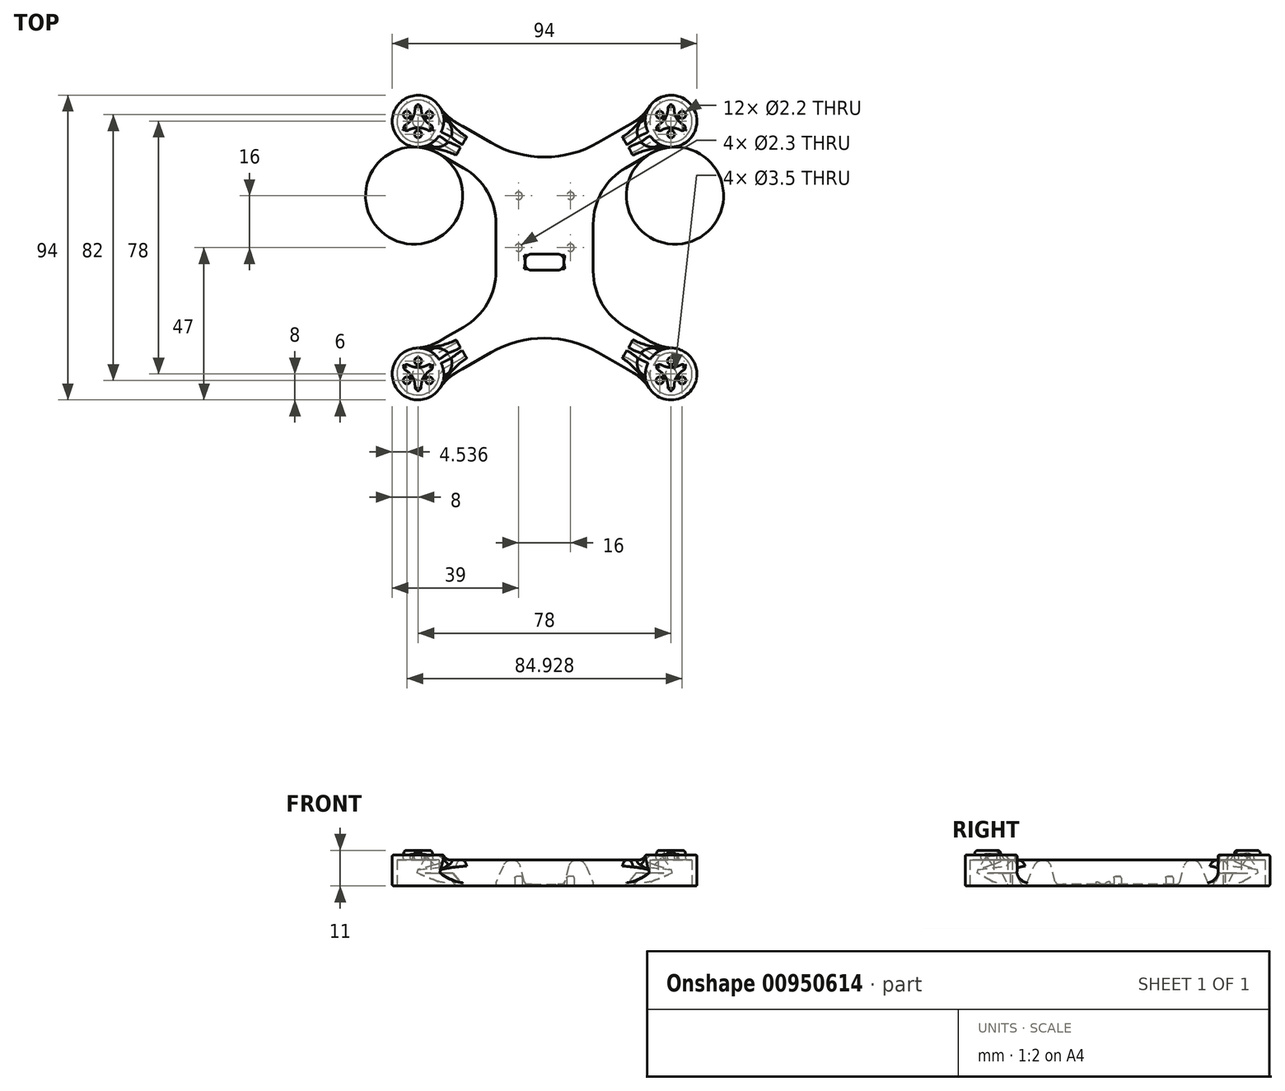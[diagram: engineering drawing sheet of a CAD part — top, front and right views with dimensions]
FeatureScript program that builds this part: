
annotation { "Feature Type Name" : "Feature", "Feature Type Description" : "" }
export const myFeature = defineFeature(function(context is Context, id is Id, definition is map)
    precondition{}
    {
        {
            var Q0;
            Q0=qCreatedBy(makeId("Top.planeOp"),FACE);
            var sketch = newSketch(context, id + "F0", { "sketchPlane" : qUnion([Q0])});
            skLineSegment(sketch, "E0", {"start": v(-31.22, 40.86) * mm, "end": v(0, 22.83) * mm});
            skLineSegment(sketch, "E1", {"start": v(0, 22.83) * mm, "end": v(31.22, 40.86) * mm});
            skLineSegment(sketch, "E2", {"start": v(-31.22, -40.86) * mm, "end": v(0, -22.83) * mm});
            skLineSegment(sketch, "E3", {"start": v(0, -22.83) * mm, "end": v(31.22, -40.86) * mm});
            skLineSegment(sketch, "E4", {"start": v(-36.72, 31.33) * mm, "end": v(-15, 18.8) * mm});
            skLineSegment(sketch, "E5", {"start": v(-15, 18.8) * mm, "end": v(-15, -18.8) * mm});
            skLineSegment(sketch, "E6", {"start": v(-15, -18.8) * mm, "end": v(-36.72, -31.33) * mm});
            skLineSegment(sketch, "E7", {"start": v(36.72, -31.33) * mm, "end": v(15, -18.8) * mm});
            skLineSegment(sketch, "E8", {"start": v(15, -18.8) * mm, "end": v(15, 18.8) * mm});
            skLineSegment(sketch, "E9", {"start": v(15, 18.8) * mm, "end": v(36.72, 31.33) * mm});
            skArc(sketch, "E10", {"start": v(-36.72, 31.33) * mm, "mid": v(-45.93, 43) * mm, "end": v(-31.22, 40.86) * mm});
            skArc(sketch, "E11", {"start": v(36.72, 31.33) * mm, "mid": v(45.93, 43) * mm, "end": v(31.22, 40.86) * mm});
            skArc(sketch, "E12", {"start": v(36.72, -31.33) * mm, "mid": v(45.93, -43) * mm, "end": v(31.22, -40.86) * mm});
            skArc(sketch, "E13", {"start": v(-36.72, -31.33) * mm, "mid": v(-45.93, -43) * mm, "end": v(-31.22, -40.86) * mm});
            skArc(sketch, "E14", {"start": v(-32.55, -38.17) * mm, "mid": v(-44.63, -42.25) * mm, "end": v(-35.05, -33.83) * mm});
            skLineSegment(sketch, "E15", {"start": v(-32.55, -38.17) * mm, "end": v(-35.05, -33.83) * mm});
            skArc(sketch, "E16", {"start": v(32.55, -38.17) * mm, "mid": v(44.63, -42.25) * mm, "end": v(35.05, -33.83) * mm});
            skArc(sketch, "E17", {"start": v(-35.05, 33.83) * mm, "mid": v(-44.63, 42.25) * mm, "end": v(-32.55, 38.17) * mm});
            skArc(sketch, "E18", {"start": v(35.05, 33.83) * mm, "mid": v(44.63, 42.25) * mm, "end": v(32.55, 38.17) * mm});
            skLineSegment(sketch, "E19", {"start": v(-35.05, 33.83) * mm, "end": v(-32.55, 38.17) * mm});
            skLineSegment(sketch, "E20", {"start": v(35.05, 33.83) * mm, "end": v(32.55, 38.17) * mm});
            skLineSegment(sketch, "E21", {"start": v(32.55, -38.17) * mm, "end": v(35.05, -33.83) * mm});
            skSolve(sketch);
        }
        {
            var Q0;
            Q0=qSketchRegion(id+"F0",true);
            extrude(context, id + "F1", {"entities" : qUnion([Q0]), "depth" : 8 * mm, "offsetDistance" : 25 * mm});
        }
        {
            var Q0;
            Q0=qCreatedBy(makeId("Front.planeOp"),FACE);
            var sketch = newSketch(context, id + "F2", { "sketchPlane" : qUnion([Q0])});
            skLineSegment(sketch, "E22.bottom", {"start": v(-6, 10.6) * mm, "end": v(6, 10.6) * mm});
            skLineSegment(sketch, "E22.top", {"start": v(-6, 0.6) * mm, "end": v(6, 0.6) * mm});
            skLineSegment(sketch, "E22.left", {"start": v(-6, 10.6) * mm, "end": v(-6, 0.6) * mm});
            skLineSegment(sketch, "E22.right", {"start": v(6, 10.6) * mm, "end": v(6, 0.6) * mm});
            skSolve(sketch);
        }
        {
            var Q0;
            Q0=qSketchRegion(id+"F2",true);
            extrude(context, id + "F3", {"entities" : qUnion([Q0]), "operationType" : NewBodyOperationType.REMOVE, "oppositeDirection" : true, "depth" : 19 * mm, "offsetDistance" : 25 * mm, "hasSecondDirection" : true, "secondDirectionOppositeDirection" : false, "secondDirectionDepth" : 19 * mm});
        }
        {
            var Q0;
            Q0=makeQuery(id+"F1.opExtrude","CAP_FACE",FACE,{"disambiguationData":[OSD([sQuery(id+"F0.wireOp",EDGE,"E0"),sQuery(id+"F0.wireOp",EDGE,"E1"),sQuery(id+"F0.wireOp",EDGE,"E2"),sQuery(id+"F0.wireOp",EDGE,"E3"),sQuery(id+"F0.wireOp",EDGE,"E4"),sQuery(id+"F0.wireOp",EDGE,"E5"),sQuery(id+"F0.wireOp",EDGE,"E6"),sQuery(id+"F0.wireOp",EDGE,"E7"),sQuery(id+"F0.wireOp",EDGE,"E8"),sQuery(id+"F0.wireOp",EDGE,"E9"),sQuery(id+"F0.wireOp",EDGE,"E10"),sQuery(id+"F0.wireOp",EDGE,"E11"),sQuery(id+"F0.wireOp",EDGE,"E12"),sQuery(id+"F0.wireOp",EDGE,"E13"),sQuery(id+"F0.wireOp",EDGE,"eY3Ntxxg-AOvC-6Sjp-1Sg7-Dh78Z1ENxIpH"),sQuery(id+"F0.wireOp",EDGE,"MyhiPNTX-cIqE-LlnS-pzt5-9fsmOIbbkCBx"),sQuery(id+"F0.wireOp",EDGE,"c5fDbUR1-X0vD-gyia-IhE2-5vfisiyByv1Z"),sQuery(id+"F0.wireOp",EDGE,"z3w7DU23-CNS4-8nrn-3kLT-20PgSTqFnzF7"),sQuery(id+"F0.wireOp",EDGE,"hVG7QURc-v0VO-WvcA-oFbQ-66XRPdHWUu1N"),sQuery(id+"F0.wireOp",EDGE,"sfXvGUbo-ry80-gNXO-uOhN-L8BNUFceVqag"),sQuery(id+"F0.wireOp",EDGE,"QFO76mAv-pKme-nUwV-aMAa-C3MPOYOEvzGl"),sQuery(id+"F0.wireOp",EDGE,"fpymSL76-tXuZ-IzAU-FBSV-KsOygqMtrIGQ")])],"isStart":false});
            var sketch = newSketch(context, id + "F4", { "sketchPlane" : qUnion([Q0])});
            skCircle(sketch, "E23", {"center": v(-39, 39) * mm, "radius": 8 * mm});
            skCircle(sketch, "E24", {"center": v(39, 39) * mm, "radius": 8 * mm});
            skCircle(sketch, "E25", {"center": v(39, -39) * mm, "radius": 8 * mm});
            skCircle(sketch, "E26", {"center": v(-39, -39) * mm, "radius": 8 * mm});
            skSolve(sketch);
        }
        {
            var Q0;
            Q0=qSketchRegion(id+"F4",true);
            extrude(context, id + "F5", {"entities" : qUnion([Q0]), "operationType" : NewBodyOperationType.ADD, "depth" : 3 * mm, "offsetDistance" : 25 * mm});
        }
        {
            var Q0;
            Q0=makeQuery(id+"F5.opExtrude","CAP_FACE",FACE,{"disambiguationData":[OSD([sQuery(id+"F4.wireOp",EDGE,"E23")])],"isStart":false});
            var sketch = newSketch(context, id + "F6", { "sketchPlane" : qUnion([Q0])});
            skCircle(sketch, "E27", {"center": v(-39, 39) * mm, "radius": 8 * mm});
            skArc(sketch, "E28", {"start": v(-43.74, 37.41) * mm, "mid": v(-40.73, 40) * mm, "end": v(-40, 43.9) * mm});
            skArc(sketch, "E29.1.0", {"start": v(-35.25, 35.69) * mm, "mid": v(-39, 37) * mm, "end": v(-42.75, 35.69) * mm});
            skArc(sketch, "E29.2.0", {"start": v(-38, 43.9) * mm, "mid": v(-37.27, 40) * mm, "end": v(-34.26, 37.41) * mm});
            skArc(sketch, "E30", {"start": v(-34.26, 37.41) * mm, "mid": v(-34.67, 36.5) * mm, "end": v(-35.25, 35.69) * mm});
            skArc(sketch, "E31", {"start": v(-38, 43.9) * mm, "mid": v(-39, 44) * mm, "end": v(-40, 43.9) * mm});
            skArc(sketch, "E32", {"start": v(-42.75, 35.69) * mm, "mid": v(-43.33, 36.5) * mm, "end": v(-43.74, 37.41) * mm});
            skCircle(sketch, "E33.MirrorC", {"center": v(39, 39) * mm, "radius": 8 * mm});
            skArc(sketch, "E34.MirrorCS", {"start": v(35.25, 35.69) * mm, "mid": v(39, 37) * mm, "end": v(42.75, 35.69) * mm});
            skArc(sketch, "E35.MirrorCS", {"start": v(34.26, 37.41) * mm, "mid": v(34.67, 36.5) * mm, "end": v(35.25, 35.69) * mm});
            skArc(sketch, "E36.MirrorCS", {"start": v(38, 43.9) * mm, "mid": v(37.27, 40) * mm, "end": v(34.26, 37.41) * mm});
            skArc(sketch, "E37.MirrorCS", {"start": v(43.74, 37.41) * mm, "mid": v(40.73, 40) * mm, "end": v(40, 43.9) * mm});
            skArc(sketch, "E38.MirrorCS", {"start": v(42.75, 35.69) * mm, "mid": v(43.33, 36.5) * mm, "end": v(43.74, 37.41) * mm});
            skArc(sketch, "E39.MirrorCS", {"start": v(38, 43.9) * mm, "mid": v(39, 44) * mm, "end": v(40, 43.9) * mm});
            skArc(sketch, "E40.MirrorCS", {"start": v(-35.25, -35.69) * mm, "mid": v(-39, -37) * mm, "end": v(-42.75, -35.69) * mm});
            skArc(sketch, "E41.MirrorCS", {"start": v(38, -43.9) * mm, "mid": v(37.27, -40) * mm, "end": v(34.26, -37.41) * mm});
            skArc(sketch, "E42.MirrorCS", {"start": v(-42.75, -35.69) * mm, "mid": v(-43.33, -36.5) * mm, "end": v(-43.74, -37.41) * mm});
            skArc(sketch, "E43.MirrorCS", {"start": v(-43.74, -37.41) * mm, "mid": v(-40.73, -40) * mm, "end": v(-40, -43.9) * mm});
            skArc(sketch, "E44.MirrorCS", {"start": v(35.25, -35.69) * mm, "mid": v(39, -37) * mm, "end": v(42.75, -35.69) * mm});
            skArc(sketch, "E45.MirrorCS", {"start": v(38, -43.9) * mm, "mid": v(39, -44) * mm, "end": v(40, -43.9) * mm});
            skArc(sketch, "E46.MirrorCS", {"start": v(-38, -43.9) * mm, "mid": v(-37.27, -40) * mm, "end": v(-34.26, -37.41) * mm});
            skArc(sketch, "E47.MirrorCS", {"start": v(43.74, -37.41) * mm, "mid": v(40.73, -40) * mm, "end": v(40, -43.9) * mm});
            skArc(sketch, "E48.MirrorCS", {"start": v(42.75, -35.69) * mm, "mid": v(43.33, -36.5) * mm, "end": v(43.74, -37.41) * mm});
            skArc(sketch, "E49.MirrorCS", {"start": v(34.26, -37.41) * mm, "mid": v(34.67, -36.5) * mm, "end": v(35.25, -35.69) * mm});
            skArc(sketch, "E50.MirrorCS", {"start": v(-38, -43.9) * mm, "mid": v(-39, -44) * mm, "end": v(-40, -43.9) * mm});
            skArc(sketch, "E51.MirrorCS", {"start": v(-34.26, -37.41) * mm, "mid": v(-34.67, -36.5) * mm, "end": v(-35.25, -35.69) * mm});
            skCircle(sketch, "E52.MirrorC", {"center": v(-39, -39) * mm, "radius": 8 * mm});
            skCircle(sketch, "E53.MirrorC", {"center": v(39, -39) * mm, "radius": 8 * mm});
            skSolve(sketch);
        }
        {
            var Q0;
            Q0 = qSketchRegion(id + "F6", true);
            extrude(context, id + "F7", {"entities" : qUnion([Q0]), "operationType" : NewBodyOperationType.REMOVE, "oppositeDirection" : true, "depth" : 1.4 * mm, "offsetDistance" : 25 * mm});
        }
        {
            var Q0;
            Q0=makeQuery(id+"F7.boolean.opBoolean","COPY",FACE,{"derivedFrom":makeQuery(id+"F7.opExtrude","CAP_FACE",FACE,{"disambiguationData":[OSD([sQuery(id+"F6.wireOp",EDGE,"E27"),sQuery(id+"F6.wireOp",EDGE,"E28"),sQuery(id+"F6.wireOp",EDGE,"E29.1.0"),sQuery(id+"F6.wireOp",EDGE,"E29.2.0"),sQuery(id+"F6.wireOp",EDGE,"E30"),sQuery(id+"F6.wireOp",EDGE,"E31"),sQuery(id+"F6.wireOp",EDGE,"E32")])],"isStart":false})});
            var sketch = newSketch(context, id + "F8", { "sketchPlane" : qUnion([Q0])});
            skCircle(sketch, "E54", {"center": v(-42.46, 41) * mm, "radius": 1.1 * mm});
            skCircle(sketch, "E55.1.0", {"center": v(-39, 35) * mm, "radius": 1.1 * mm});
            skCircle(sketch, "E55.2.0", {"center": v(-35.54, 41) * mm, "radius": 1.1 * mm});
            skPoint(sketch, "E55.center", {"position": v(-39, 39) * mm});
            skCircle(sketch, "E56.MirrorC", {"center": v(39, 35) * mm, "radius": 1.1 * mm});
            skCircle(sketch, "E57.MirrorC", {"center": v(35.54, 41) * mm, "radius": 1.1 * mm});
            skCircle(sketch, "E58.MirrorC", {"center": v(42.46, 41) * mm, "radius": 1.1 * mm});
            skPoint(sketch, "E59.MirrorP", {"position": v(39, 39) * mm});
            skCircle(sketch, "E60.MirrorC", {"center": v(-35.54, -41) * mm, "radius": 1.1 * mm});
            skCircle(sketch, "E61.MirrorC", {"center": v(-42.46, -41) * mm, "radius": 1.1 * mm});
            skCircle(sketch, "E62.MirrorC", {"center": v(35.54, -41) * mm, "radius": 1.1 * mm});
            skCircle(sketch, "E63.MirrorC", {"center": v(42.46, -41) * mm, "radius": 1.1 * mm});
            skCircle(sketch, "E64.MirrorC", {"center": v(-39, -35) * mm, "radius": 1.1 * mm});
            skCircle(sketch, "E65.MirrorC", {"center": v(39, -35) * mm, "radius": 1.1 * mm});
            skPoint(sketch, "E66.MirrorP", {"position": v(39, -39) * mm});
            skPoint(sketch, "E67.MirrorP", {"position": v(-39, -39) * mm});
            skSolve(sketch);
        }
        {
            var Q0;
            Q0 = qSketchRegion(id + "F8", true);
            extrude(context, id + "F9", {"entities" : qUnion([Q0]), "operationType" : NewBodyOperationType.REMOVE, "oppositeDirection" : true, "depth" : 3 * mm, "offsetDistance" : 25 * mm});
        }
        {
            var Q0;
            Q0=qCreatedBy(makeId("Top.planeOp"),FACE);
            var sketch = newSketch(context, id + "F10", { "sketchPlane" : qUnion([Q0])});
            skCircle(sketch, "E68", {"center": v(8, 16) * mm, "radius": 1.15 * mm});
            skCircle(sketch, "E69", {"center": v(-8, 16) * mm, "radius": 1.15 * mm});
            skCircle(sketch, "E70", {"center": v(-8, 0) * mm, "radius": 1.15 * mm});
            skCircle(sketch, "E71", {"center": v(8, 0) * mm, "radius": 1.15 * mm});
            skLineSegment(sketch, "E72.bottom", {"start": v(-4, -7) * mm, "end": v(4, -7) * mm});
            skLineSegment(sketch, "E72.top", {"start": v(-4, -2) * mm, "end": v(4, -2) * mm});
            skLineSegment(sketch, "E72.left", {"start": v(-6, -5) * mm, "end": v(-6, -4) * mm});
            skLineSegment(sketch, "E72.right", {"start": v(6, -5) * mm, "end": v(6, -4) * mm});
            skPoint(sketch, "E73.visualSharp", {"position": v(-6, -7) * mm});
            skArc(sketch, "E73.filletArc", {"start": v(-6, -5) * mm, "mid": v(-5.41, -6.41) * mm, "end": v(-4, -7) * mm});
            skPoint(sketch, "E74.visualSharp", {"position": v(-6, -2) * mm});
            skArc(sketch, "E74.filletArc", {"start": v(-4, -2) * mm, "mid": v(-5.41, -2.59) * mm, "end": v(-6, -4) * mm});
            skPoint(sketch, "E75.visualSharp", {"position": v(6, -7) * mm});
            skArc(sketch, "E75.filletArc", {"start": v(4, -7) * mm, "mid": v(5.41, -6.41) * mm, "end": v(6, -5) * mm});
            skPoint(sketch, "E76.visualSharp", {"position": v(6, -2) * mm});
            skArc(sketch, "E76.filletArc", {"start": v(6, -4) * mm, "mid": v(5.41, -2.59) * mm, "end": v(4, -2) * mm});
            skSolve(sketch);
        }
        {
            var Q0;
            Q0 = qSketchRegion(id + "F10", true);
            extrude(context, id + "F11", {"entities" : qUnion([Q0]), "operationType" : NewBodyOperationType.REMOVE, "depth" : 3 * mm, "offsetDistance" : 25 * mm});
        }
        {
            var Q0;
            Q0=makeQuery(id+"F5.opExtrude","CAP_FACE",FACE,{"disambiguationData":[OSD([sQuery(id+"F4.wireOp",EDGE,"E26")])],"isStart":true});
            var sketch = newSketch(context, id + "F12", { "sketchPlane" : qUnion([Q0])});
            skCircle(sketch, "E77", {"center": v(-39, 39) * mm, "radius": 1.75 * mm});
            skCircle(sketch, "E78.MirrorC", {"center": v(39, 39) * mm, "radius": 1.75 * mm});
            skCircle(sketch, "E79.MirrorC", {"center": v(-39, -39) * mm, "radius": 1.75 * mm});
            skCircle(sketch, "E80.MirrorC", {"center": v(39, -39) * mm, "radius": 1.75 * mm});
            skSolve(sketch);
        }
        {
            var Q0;
            Q0 = qSketchRegion(id + "F12", true);
            extrude(context, id + "F13", {"entities" : qUnion([Q0]), "operationType" : NewBodyOperationType.REMOVE, "oppositeDirection" : true, "depth" : 2 * mm, "offsetDistance" : 25 * mm});
        }
        {
            var Q0;
            Q0=qCreatedBy(makeId("Top.planeOp"),FACE);
            var sketch = newSketch(context, id + "F14", { "sketchPlane" : qUnion([Q0])});
            skLineSegment(sketch, "E81", {"start": v(-32.55, -38.17) * mm, "end": v(-23.9, -33.17) * mm});
            skLineSegment(sketch, "E82", {"start": v(-23.9, -33.17) * mm, "end": v(-26.4, -28.83) * mm});
            skLineSegment(sketch, "E83", {"start": v(-26.4, -28.83) * mm, "end": v(-35.05, -33.83) * mm});
            skLineSegment(sketch, "E84", {"start": v(-35.05, -33.83) * mm, "end": v(-32.55, -38.17) * mm});
            skLineSegment(sketch, "E85.MirrorCS", {"start": v(-23.9, 33.17) * mm, "end": v(-26.4, 28.83) * mm});
            skLineSegment(sketch, "E86.MirrorCS", {"start": v(-32.55, 38.17) * mm, "end": v(-23.9, 33.17) * mm});
            skLineSegment(sketch, "E87.MirrorCS", {"start": v(-35.05, 33.83) * mm, "end": v(-32.55, 38.17) * mm});
            skLineSegment(sketch, "E88.MirrorCS", {"start": v(-26.4, 28.83) * mm, "end": v(-35.05, 33.83) * mm});
            skLineSegment(sketch, "E89.MirrorCS", {"start": v(35.05, -33.83) * mm, "end": v(32.55, -38.17) * mm});
            skLineSegment(sketch, "E90.MirrorCS", {"start": v(35.05, 33.83) * mm, "end": v(32.55, 38.17) * mm});
            skLineSegment(sketch, "E91.MirrorCS", {"start": v(23.9, -33.17) * mm, "end": v(26.4, -28.83) * mm});
            skLineSegment(sketch, "E92.MirrorCS", {"start": v(23.9, 33.17) * mm, "end": v(26.4, 28.83) * mm});
            skLineSegment(sketch, "E93.MirrorCS", {"start": v(32.55, -38.17) * mm, "end": v(23.9, -33.17) * mm});
            skLineSegment(sketch, "E94.MirrorCS", {"start": v(26.4, -28.83) * mm, "end": v(35.05, -33.83) * mm});
            skLineSegment(sketch, "E95.MirrorCS", {"start": v(26.4, 28.83) * mm, "end": v(35.05, 33.83) * mm});
            skLineSegment(sketch, "E96.MirrorCS", {"start": v(32.55, 38.17) * mm, "end": v(23.9, 33.17) * mm});
            skSolve(sketch);
        }
        {
            var Q0;
            Q0 = qSketchRegion(id + "F14", true);
            extrude(context, id + "F15", {"entities" : qUnion([Q0]), "operationType" : NewBodyOperationType.REMOVE, "depth" : 4 * mm, "offsetDistance" : 25 * mm});
        }
        {
            var Q0;
            Q0=makeQuery(id+"F15.boolean.opBoolean","COPY",EDGE,{"derivedFrom":makeQuery(id+"F15.opExtrude","CAP_EDGE",EDGE,{"disambiguationData":[OSD([sQuery(id+"F14.wireOp",EDGE,"E84")])],"isStart":false})});
            var Q1;
            Q1=makeQuery(id+"F15.boolean.opBoolean","COPY",EDGE,{"derivedFrom":makeQuery(id+"F15.opExtrude","CAP_EDGE",EDGE,{"disambiguationData":[OSD([sQuery(id+"F14.wireOp",EDGE,"E82")])],"isStart":false})});
            var Q2;
            Q2=makeQuery(id+"F15.boolean.opBoolean","COPY",EDGE,{"derivedFrom":makeQuery(id+"F15.opExtrude","CAP_EDGE",EDGE,{"disambiguationData":[OSD([sQuery(id+"F14.wireOp",EDGE,"E91.MirrorCS")])],"isStart":false})});
            var Q3;
            Q3=makeQuery(id+"F15.boolean.opBoolean","COPY",EDGE,{"derivedFrom":makeQuery(id+"F15.opExtrude","CAP_EDGE",EDGE,{"disambiguationData":[OSD([sQuery(id+"F14.wireOp",EDGE,"E89.MirrorCS")])],"isStart":false})});
            var Q4;
            Q4=makeQuery(id+"F15.boolean.opBoolean","COPY",EDGE,{"derivedFrom":makeQuery(id+"F15.opExtrude","CAP_EDGE",EDGE,{"disambiguationData":[OSD([sQuery(id+"F14.wireOp",EDGE,"E92.MirrorCS")])],"isStart":false})});
            var Q5;
            Q5=makeQuery(id+"F15.boolean.opBoolean","COPY",EDGE,{"derivedFrom":makeQuery(id+"F15.opExtrude","CAP_EDGE",EDGE,{"disambiguationData":[OSD([sQuery(id+"F14.wireOp",EDGE,"E90.MirrorCS")])],"isStart":false})});
            var Q6;
            Q6=makeQuery(id+"F15.boolean.opBoolean","COPY",EDGE,{"derivedFrom":makeQuery(id+"F15.opExtrude","CAP_EDGE",EDGE,{"disambiguationData":[OSD([sQuery(id+"F14.wireOp",EDGE,"E87.MirrorCS")])],"isStart":false})});
            var Q7;
            Q7=makeQuery(id+"F15.boolean.opBoolean","COPY",EDGE,{"derivedFrom":makeQuery(id+"F15.opExtrude","CAP_EDGE",EDGE,{"disambiguationData":[OSD([sQuery(id+"F14.wireOp",EDGE,"E85.MirrorCS")])],"isStart":false})});
            chamfer(context, id + "F16", {"entities" : qUnion([Q0, Q1, Q2, Q3, Q4, Q5, Q6, Q7]), "width" : 5 * mm, "tangentPropagation" : true});
        }
        {
            var Q0;
            Q0=makeQuery(id+"F1.opExtrude","SWEPT_EDGE",EDGE,{"disambiguationData":[OSD([sQuery(id+"F0.wireOp",EDGE,"E0"),sQuery(id+"F0.wireOp",EDGE,"E1")])]});
            var Q1;
            Q1=makeQuery(id+"F1.opExtrude","SWEPT_EDGE",EDGE,{"disambiguationData":[OSD([sQuery(id+"F0.wireOp",EDGE,"E2"),sQuery(id+"F0.wireOp",EDGE,"E3")])]});
            fillet(context, id + "F17", {"entities" : qUnion([Q0, Q1]), "radius" : 33 * mm, "tangentPropagation" : true, "allowEdgeOverflow" : false});
        }
        {
            var Q0;
            Q0=makeQuery(id+"F1.opExtrude","SWEPT_EDGE",EDGE,{"disambiguationData":[OSD([sQuery(id+"F0.wireOp",EDGE,"E4"),sQuery(id+"F0.wireOp",EDGE,"E5")])]});
            var Q1;
            Q1=makeQuery(id+"F1.opExtrude","SWEPT_EDGE",EDGE,{"disambiguationData":[OSD([sQuery(id+"F0.wireOp",EDGE,"E5"),sQuery(id+"F0.wireOp",EDGE,"E6")])]});
            var Q2;
            Q2=makeQuery(id+"F1.opExtrude","SWEPT_EDGE",EDGE,{"disambiguationData":[OSD([sQuery(id+"F0.wireOp",EDGE,"E8"),sQuery(id+"F0.wireOp",EDGE,"E9")])]});
            var Q3;
            Q3=makeQuery(id+"F1.opExtrude","SWEPT_EDGE",EDGE,{"disambiguationData":[OSD([sQuery(id+"F0.wireOp",EDGE,"E7"),sQuery(id+"F0.wireOp",EDGE,"E8")])]});
            fillet(context, id + "F18", {"entities" : qUnion([Q0, Q1, Q2, Q3]), "radius" : 20 * mm, "tangentPropagation" : true, "allowEdgeOverflow" : false});
        }
        {
            var Q0;
            Q0=makeQuery(id+"F1.opExtrude","CAP_EDGE",EDGE,{"disambiguationData":[OSD([sQuery(id+"F0.wireOp",EDGE,"E2")])],"isStart":false});
            var Q1;
            Q1=makeQuery(id+"F1.opExtrude","CAP_EDGE",EDGE,{"disambiguationData":[OSD([sQuery(id+"F0.wireOp",EDGE,"E6")])],"isStart":false});
            var Q2;
            Q2=makeQuery(id+"F1.opExtrude","CAP_EDGE",EDGE,{"disambiguationData":[OSD([sQuery(id+"F0.wireOp",EDGE,"E3")])],"isStart":false});
            var Q3;
            Q3=makeQuery(id+"F1.opExtrude","CAP_EDGE",EDGE,{"disambiguationData":[OSD([sQuery(id+"F0.wireOp",EDGE,"E7")])],"isStart":false});
            var Q4;
            Q4=makeQuery(id+"F1.opExtrude","CAP_EDGE",EDGE,{"disambiguationData":[OSD([sQuery(id+"F0.wireOp",EDGE,"E1")])],"isStart":false});
            var Q5;
            Q5=makeQuery(id+"F1.opExtrude","CAP_EDGE",EDGE,{"disambiguationData":[OSD([sQuery(id+"F0.wireOp",EDGE,"E0")])],"isStart":false});
            var Q6;
            Q6=makeQuery(id+"F1.opExtrude","CAP_EDGE",EDGE,{"disambiguationData":[OSD([sQuery(id+"F0.wireOp",EDGE,"E4")])],"isStart":false});
            var Q7;
            Q7=makeQuery(id+"F1.opExtrude","CAP_EDGE",EDGE,{"disambiguationData":[OSD([sQuery(id+"F0.wireOp",EDGE,"E9")])],"isStart":false});
            chamfer(context, id + "F19", {"entities" : qUnion([Q0, Q1, Q2, Q3, Q4, Q5, Q6, Q7]), "chamferType" : ChamferType.TWO_OFFSETS, "width1" : 3 * mm, "oppositeDirection" : false, "width2" : 7 * mm, "tangentPropagation" : true});
        }
        {
            var Q0;
            Q0=makeQuery(id+"F3.boolean.opBoolean","COPY",EDGE,{"derivedFrom":makeQuery(id+"F3.opExtrude","CAP_EDGE",EDGE,{"disambiguationData":[OSD([sQuery(id+"F2.wireOp",EDGE,"E22.left")])],"isStart":false})});
            var Q1;
            Q1=makeQuery(id+"F3.boolean.opBoolean","COPY",EDGE,{"derivedFrom":makeQuery(id+"F3.opExtrude","CAP_EDGE",EDGE,{"disambiguationData":[OSD([sQuery(id+"F2.wireOp",EDGE,"E22.right")])],"isStart":false})});
            var Q2;
            Q2=makeQuery(id+"F3.boolean.opBoolean","COPY",EDGE,{"derivedFrom":makeQuery(id+"F3.opExtrude","CAP_EDGE",EDGE,{"disambiguationData":[OSD([sQuery(id+"F2.wireOp",EDGE,"E22.left")])],"isStart":true})});
            var Q3;
            Q3=makeQuery(id+"F3.boolean.opBoolean","COPY",EDGE,{"derivedFrom":makeQuery(id+"F3.opExtrude","CAP_EDGE",EDGE,{"disambiguationData":[OSD([sQuery(id+"F2.wireOp",EDGE,"E22.right")])],"isStart":true})});
            fillet(context, id + "F20", {"entities" : qUnion([Q0, Q1, Q2, Q3]), "radius" : 2 * mm, "tangentPropagation" : true, "allowEdgeOverflow" : false});
        }
        {
            var Q0;
            Q0=makeQuery(id+"F3.boolean.opBoolean","INTERSECT",EDGE,{"derivedFrom":[makeQuery(id+"F1.opExtrude","CAP_FACE",FACE,{"disambiguationData":[OSD([sQuery(id+"F0.wireOp",EDGE,"E0"),sQuery(id+"F0.wireOp",EDGE,"E1"),sQuery(id+"F0.wireOp",EDGE,"E2"),sQuery(id+"F0.wireOp",EDGE,"E3"),sQuery(id+"F0.wireOp",EDGE,"E4"),sQuery(id+"F0.wireOp",EDGE,"E5"),sQuery(id+"F0.wireOp",EDGE,"E6"),sQuery(id+"F0.wireOp",EDGE,"E7"),sQuery(id+"F0.wireOp",EDGE,"E8"),sQuery(id+"F0.wireOp",EDGE,"E9"),sQuery(id+"F0.wireOp",EDGE,"E10"),sQuery(id+"F0.wireOp",EDGE,"E11"),sQuery(id+"F0.wireOp",EDGE,"E12"),sQuery(id+"F0.wireOp",EDGE,"E13"),sQuery(id+"F0.wireOp",EDGE,"eY3Ntxxg-AOvC-6Sjp-1Sg7-Dh78Z1ENxIpH"),sQuery(id+"F0.wireOp",EDGE,"MyhiPNTX-cIqE-LlnS-pzt5-9fsmOIbbkCBx"),sQuery(id+"F0.wireOp",EDGE,"c5fDbUR1-X0vD-gyia-IhE2-5vfisiyByv1Z"),sQuery(id+"F0.wireOp",EDGE,"z3w7DU23-CNS4-8nrn-3kLT-20PgSTqFnzF7"),sQuery(id+"F0.wireOp",EDGE,"hVG7QURc-v0VO-WvcA-oFbQ-66XRPdHWUu1N"),sQuery(id+"F0.wireOp",EDGE,"sfXvGUbo-ry80-gNXO-uOhN-L8BNUFceVqag"),sQuery(id+"F0.wireOp",EDGE,"QFO76mAv-pKme-nUwV-aMAa-C3MPOYOEvzGl"),sQuery(id+"F0.wireOp",EDGE,"fpymSL76-tXuZ-IzAU-FBSV-KsOygqMtrIGQ"),sQuery(id+"F0.wireOp",EDGE,"9a1d0dfd-7d57-477c-bff2-5a3fdc463cc7.filletArc"),sQuery(id+"F0.wireOp",EDGE,"38622195-8d8f-4664-a9bd-1ddf4e6b9831.filletArc"),sQuery(id+"F0.wireOp",EDGE,"98761a0e-d686-4a46-9134-fa1f6f4434ea.filletArc"),sQuery(id+"F0.wireOp",EDGE,"828cccf2-c6bf-4f99-963a-41c4c980739f.filletArc"),sQuery(id+"F0.wireOp",EDGE,"103ca256-2ef9-437d-bf9e-3dfbfe53d8ef.filletArc"),sQuery(id+"F0.wireOp",EDGE,"ed541100-cfe0-4745-a776-ba2087af7cae.filletArc"),sQuery(id+"F0.wireOp",EDGE,"bcec124a-270f-4962-9b0e-bfe1ee30ba45.filletArc"),sQuery(id+"F0.wireOp",EDGE,"ffb815b5-0439-4a1d-8740-96b920259a73.filletArc")])],"isStart":false}),makeQuery(id+"F3.opExtrude","CAP_FACE",FACE,{"disambiguationData":[OSD([sQuery(id+"F2.wireOp",EDGE,"E22.bottom"),sQuery(id+"F2.wireOp",EDGE,"E22.top"),sQuery(id+"F2.wireOp",EDGE,"E22.left"),sQuery(id+"F2.wireOp",EDGE,"E22.right")])],"isStart":false})]});
            chamfer(context, id + "F21", {"entities" : qUnion([Q0]), "chamferType" : ChamferType.TWO_OFFSETS, "width1" : 2 * mm, "oppositeDirection" : false, "width2" : 7.4 * mm, "tangentPropagation" : true});
        }
        {
            var Q0;
            Q0=makeQuery(id+"F19.opChamfer","BLEND_EDGE",EDGE,{"blendedFrom":[makeQuery(id+"F1.opExtrude","CAP_EDGE",EDGE,{"disambiguationData":[OSD([sQuery(id+"F0.wireOp",EDGE,"E9")])],"isStart":false}),makeQuery(id+"F5.boolean.opBoolean","MERGE",FACE,{"derivedFrom":[makeQuery(id+"F1.opExtrude","SWEPT_FACE",FACE,{"disambiguationData":[OSD([sQuery(id+"F0.wireOp",EDGE,"E11")])]}),makeQuery(id+"F5.opExtrude","SWEPT_FACE",FACE,{"disambiguationData":[OSD([sQuery(id+"F4.wireOp",EDGE,"E24")])]})]})],"blendedInto":[makeQuery(id+"F5.boolean.opBoolean","MERGE",FACE,{"derivedFrom":[makeQuery(id+"F1.opExtrude","SWEPT_FACE",FACE,{"disambiguationData":[OSD([sQuery(id+"F0.wireOp",EDGE,"E11")])]}),makeQuery(id+"F5.opExtrude","SWEPT_FACE",FACE,{"disambiguationData":[OSD([sQuery(id+"F4.wireOp",EDGE,"E24")])]})]})]});
            var Q1;
            Q1=makeQuery(id+"F1.opExtrude","SWEPT_EDGE",EDGE,{"disambiguationData":[OSD([sQuery(id+"F0.wireOp",EDGE,"E9"),sQuery(id+"F0.wireOp",EDGE,"E11")])]});
            var Q2;
            Q2=makeQuery(id+"F1.opExtrude","SWEPT_EDGE",EDGE,{"disambiguationData":[OSD([sQuery(id+"F0.wireOp",EDGE,"E1"),sQuery(id+"F0.wireOp",EDGE,"E11")])]});
            var Q3;
            Q3=makeQuery(id+"F19.opChamfer","BLEND_EDGE",EDGE,{"blendedFrom":[makeQuery(id+"F1.opExtrude","CAP_EDGE",EDGE,{"disambiguationData":[OSD([sQuery(id+"F0.wireOp",EDGE,"E1")])],"isStart":false}),makeQuery(id+"F5.boolean.opBoolean","MERGE",FACE,{"derivedFrom":[makeQuery(id+"F1.opExtrude","SWEPT_FACE",FACE,{"disambiguationData":[OSD([sQuery(id+"F0.wireOp",EDGE,"E11")])]}),makeQuery(id+"F5.opExtrude","SWEPT_FACE",FACE,{"disambiguationData":[OSD([sQuery(id+"F4.wireOp",EDGE,"E24")])]})]})],"blendedInto":[makeQuery(id+"F5.boolean.opBoolean","MERGE",FACE,{"derivedFrom":[makeQuery(id+"F1.opExtrude","SWEPT_FACE",FACE,{"disambiguationData":[OSD([sQuery(id+"F0.wireOp",EDGE,"E11")])]}),makeQuery(id+"F5.opExtrude","SWEPT_FACE",FACE,{"disambiguationData":[OSD([sQuery(id+"F4.wireOp",EDGE,"E24")])]})]})]});
            var Q4;
            Q4=makeQuery(id+"F1.opExtrude","SWEPT_EDGE",EDGE,{"disambiguationData":[OSD([sQuery(id+"F0.wireOp",EDGE,"E0"),sQuery(id+"F0.wireOp",EDGE,"E10")])]});
            var Q5;
            Q5=makeQuery(id+"F19.opChamfer","BLEND_EDGE",EDGE,{"blendedFrom":[makeQuery(id+"F1.opExtrude","CAP_EDGE",EDGE,{"disambiguationData":[OSD([sQuery(id+"F0.wireOp",EDGE,"E0")])],"isStart":false}),makeQuery(id+"F5.boolean.opBoolean","MERGE",FACE,{"derivedFrom":[makeQuery(id+"F1.opExtrude","SWEPT_FACE",FACE,{"disambiguationData":[OSD([sQuery(id+"F0.wireOp",EDGE,"E10")])]}),makeQuery(id+"F5.opExtrude","SWEPT_FACE",FACE,{"disambiguationData":[OSD([sQuery(id+"F4.wireOp",EDGE,"E23")])]})]})],"blendedInto":[makeQuery(id+"F5.boolean.opBoolean","MERGE",FACE,{"derivedFrom":[makeQuery(id+"F1.opExtrude","SWEPT_FACE",FACE,{"disambiguationData":[OSD([sQuery(id+"F0.wireOp",EDGE,"E10")])]}),makeQuery(id+"F5.opExtrude","SWEPT_FACE",FACE,{"disambiguationData":[OSD([sQuery(id+"F4.wireOp",EDGE,"E23")])]})]})]});
            var Q6;
            Q6=makeQuery(id+"F19.opChamfer","BLEND_EDGE",EDGE,{"blendedFrom":[makeQuery(id+"F1.opExtrude","CAP_EDGE",EDGE,{"disambiguationData":[OSD([sQuery(id+"F0.wireOp",EDGE,"E4")])],"isStart":false}),makeQuery(id+"F5.boolean.opBoolean","MERGE",FACE,{"derivedFrom":[makeQuery(id+"F1.opExtrude","SWEPT_FACE",FACE,{"disambiguationData":[OSD([sQuery(id+"F0.wireOp",EDGE,"E10")])]}),makeQuery(id+"F5.opExtrude","SWEPT_FACE",FACE,{"disambiguationData":[OSD([sQuery(id+"F4.wireOp",EDGE,"E23")])]})]})],"blendedInto":[makeQuery(id+"F5.boolean.opBoolean","MERGE",FACE,{"derivedFrom":[makeQuery(id+"F1.opExtrude","SWEPT_FACE",FACE,{"disambiguationData":[OSD([sQuery(id+"F0.wireOp",EDGE,"E10")])]}),makeQuery(id+"F5.opExtrude","SWEPT_FACE",FACE,{"disambiguationData":[OSD([sQuery(id+"F4.wireOp",EDGE,"E23")])]})]})]});
            var Q7;
            Q7=makeQuery(id+"F1.opExtrude","SWEPT_EDGE",EDGE,{"disambiguationData":[OSD([sQuery(id+"F0.wireOp",EDGE,"E4"),sQuery(id+"F0.wireOp",EDGE,"E10")])]});
            var Q8;
            Q8=makeQuery(id+"F19.opChamfer","BLEND_EDGE",EDGE,{"blendedFrom":[makeQuery(id+"F1.opExtrude","CAP_EDGE",EDGE,{"disambiguationData":[OSD([sQuery(id+"F0.wireOp",EDGE,"E2")])],"isStart":false}),makeQuery(id+"F5.boolean.opBoolean","MERGE",FACE,{"derivedFrom":[makeQuery(id+"F1.opExtrude","SWEPT_FACE",FACE,{"disambiguationData":[OSD([sQuery(id+"F0.wireOp",EDGE,"E13")])]}),makeQuery(id+"F5.opExtrude","SWEPT_FACE",FACE,{"disambiguationData":[OSD([sQuery(id+"F4.wireOp",EDGE,"E26")])]})]})],"blendedInto":[makeQuery(id+"F5.boolean.opBoolean","MERGE",FACE,{"derivedFrom":[makeQuery(id+"F1.opExtrude","SWEPT_FACE",FACE,{"disambiguationData":[OSD([sQuery(id+"F0.wireOp",EDGE,"E13")])]}),makeQuery(id+"F5.opExtrude","SWEPT_FACE",FACE,{"disambiguationData":[OSD([sQuery(id+"F4.wireOp",EDGE,"E26")])]})]})]});
            var Q9;
            Q9=makeQuery(id+"F1.opExtrude","SWEPT_EDGE",EDGE,{"disambiguationData":[OSD([sQuery(id+"F0.wireOp",EDGE,"E2"),sQuery(id+"F0.wireOp",EDGE,"E13")])]});
            var Q10;
            Q10=makeQuery(id+"F19.opChamfer","BLEND_EDGE",EDGE,{"blendedFrom":[makeQuery(id+"F1.opExtrude","CAP_EDGE",EDGE,{"disambiguationData":[OSD([sQuery(id+"F0.wireOp",EDGE,"E6")])],"isStart":false}),makeQuery(id+"F5.boolean.opBoolean","MERGE",FACE,{"derivedFrom":[makeQuery(id+"F1.opExtrude","SWEPT_FACE",FACE,{"disambiguationData":[OSD([sQuery(id+"F0.wireOp",EDGE,"E13")])]}),makeQuery(id+"F5.opExtrude","SWEPT_FACE",FACE,{"disambiguationData":[OSD([sQuery(id+"F4.wireOp",EDGE,"E26")])]})]})],"blendedInto":[makeQuery(id+"F5.boolean.opBoolean","MERGE",FACE,{"derivedFrom":[makeQuery(id+"F1.opExtrude","SWEPT_FACE",FACE,{"disambiguationData":[OSD([sQuery(id+"F0.wireOp",EDGE,"E13")])]}),makeQuery(id+"F5.opExtrude","SWEPT_FACE",FACE,{"disambiguationData":[OSD([sQuery(id+"F4.wireOp",EDGE,"E26")])]})]})]});
            var Q11;
            Q11=makeQuery(id+"F1.opExtrude","SWEPT_EDGE",EDGE,{"disambiguationData":[OSD([sQuery(id+"F0.wireOp",EDGE,"E6"),sQuery(id+"F0.wireOp",EDGE,"E13")])]});
            var Q12;
            Q12=makeQuery(id+"F19.opChamfer","BLEND_EDGE",EDGE,{"blendedFrom":[makeQuery(id+"F1.opExtrude","CAP_EDGE",EDGE,{"disambiguationData":[OSD([sQuery(id+"F0.wireOp",EDGE,"E7")])],"isStart":false}),makeQuery(id+"F5.boolean.opBoolean","MERGE",FACE,{"derivedFrom":[makeQuery(id+"F1.opExtrude","SWEPT_FACE",FACE,{"disambiguationData":[OSD([sQuery(id+"F0.wireOp",EDGE,"E12")])]}),makeQuery(id+"F5.opExtrude","SWEPT_FACE",FACE,{"disambiguationData":[OSD([sQuery(id+"F4.wireOp",EDGE,"E25")])]})]})],"blendedInto":[makeQuery(id+"F5.boolean.opBoolean","MERGE",FACE,{"derivedFrom":[makeQuery(id+"F1.opExtrude","SWEPT_FACE",FACE,{"disambiguationData":[OSD([sQuery(id+"F0.wireOp",EDGE,"E12")])]}),makeQuery(id+"F5.opExtrude","SWEPT_FACE",FACE,{"disambiguationData":[OSD([sQuery(id+"F4.wireOp",EDGE,"E25")])]})]})]});
            var Q13;
            Q13=makeQuery(id+"F1.opExtrude","SWEPT_EDGE",EDGE,{"disambiguationData":[OSD([sQuery(id+"F0.wireOp",EDGE,"E7"),sQuery(id+"F0.wireOp",EDGE,"E12")])]});
            var Q14;
            Q14=makeQuery(id+"F19.opChamfer","BLEND_EDGE",EDGE,{"blendedFrom":[makeQuery(id+"F1.opExtrude","CAP_EDGE",EDGE,{"disambiguationData":[OSD([sQuery(id+"F0.wireOp",EDGE,"E3")])],"isStart":false}),makeQuery(id+"F5.boolean.opBoolean","MERGE",FACE,{"derivedFrom":[makeQuery(id+"F1.opExtrude","SWEPT_FACE",FACE,{"disambiguationData":[OSD([sQuery(id+"F0.wireOp",EDGE,"E12")])]}),makeQuery(id+"F5.opExtrude","SWEPT_FACE",FACE,{"disambiguationData":[OSD([sQuery(id+"F4.wireOp",EDGE,"E25")])]})]})],"blendedInto":[makeQuery(id+"F5.boolean.opBoolean","MERGE",FACE,{"derivedFrom":[makeQuery(id+"F1.opExtrude","SWEPT_FACE",FACE,{"disambiguationData":[OSD([sQuery(id+"F0.wireOp",EDGE,"E12")])]}),makeQuery(id+"F5.opExtrude","SWEPT_FACE",FACE,{"disambiguationData":[OSD([sQuery(id+"F4.wireOp",EDGE,"E25")])]})]})]});
            var Q15;
            Q15=makeQuery(id+"F1.opExtrude","SWEPT_EDGE",EDGE,{"disambiguationData":[OSD([sQuery(id+"F0.wireOp",EDGE,"E3"),sQuery(id+"F0.wireOp",EDGE,"E12")])]});
            fillet(context, id + "F22", {"entities" : qUnion([Q0, Q1, Q2, Q3, Q4, Q5, Q6, Q7, Q8, Q9, Q10, Q11, Q12, Q13, Q14, Q15]), "radius" : 15 * mm, "tangentPropagation" : true, "allowEdgeOverflow" : false});
        }
        {
            var Q0;
            {var subQ0=sQuery(id+"F0.wireOp",EDGE,"E3");var subQ1=sQuery(id+"F0.wireOp",EDGE,"E2");Q0=makeQuery(id+"F19.opChamfer","BLEND_EDGE",EDGE,{"blendedFrom":[makeQuery(id+"F17.opFillet","BLEND_EDGE",EDGE,{"blendedFrom":[makeQuery(id+"F1.opExtrude","SWEPT_EDGE",EDGE,{"disambiguationData":[OSD([subQ1,subQ0])]}),makeQuery(id+"F1.opExtrude","CAP_FACE",FACE,{"disambiguationData":[OSD([sQuery(id+"F0.wireOp",EDGE,"E0"),sQuery(id+"F0.wireOp",EDGE,"E1"),subQ1,subQ0,sQuery(id+"F0.wireOp",EDGE,"E4"),sQuery(id+"F0.wireOp",EDGE,"E5"),sQuery(id+"F0.wireOp",EDGE,"E6"),sQuery(id+"F0.wireOp",EDGE,"E7"),sQuery(id+"F0.wireOp",EDGE,"E8"),sQuery(id+"F0.wireOp",EDGE,"E9"),sQuery(id+"F0.wireOp",EDGE,"E10"),sQuery(id+"F0.wireOp",EDGE,"E11"),sQuery(id+"F0.wireOp",EDGE,"E12"),sQuery(id+"F0.wireOp",EDGE,"E13"),sQuery(id+"F0.wireOp",EDGE,"eY3Ntxxg-AOvC-6Sjp-1Sg7-Dh78Z1ENxIpH"),sQuery(id+"F0.wireOp",EDGE,"MyhiPNTX-cIqE-LlnS-pzt5-9fsmOIbbkCBx"),sQuery(id+"F0.wireOp",EDGE,"c5fDbUR1-X0vD-gyia-IhE2-5vfisiyByv1Z"),sQuery(id+"F0.wireOp",EDGE,"z3w7DU23-CNS4-8nrn-3kLT-20PgSTqFnzF7"),sQuery(id+"F0.wireOp",EDGE,"hVG7QURc-v0VO-WvcA-oFbQ-66XRPdHWUu1N"),sQuery(id+"F0.wireOp",EDGE,"sfXvGUbo-ry80-gNXO-uOhN-L8BNUFceVqag"),sQuery(id+"F0.wireOp",EDGE,"QFO76mAv-pKme-nUwV-aMAa-C3MPOYOEvzGl"),sQuery(id+"F0.wireOp",EDGE,"fpymSL76-tXuZ-IzAU-FBSV-KsOygqMtrIGQ"),sQuery(id+"F0.wireOp",EDGE,"9a1d0dfd-7d57-477c-bff2-5a3fdc463cc7.filletArc"),sQuery(id+"F0.wireOp",EDGE,"38622195-8d8f-4664-a9bd-1ddf4e6b9831.filletArc"),sQuery(id+"F0.wireOp",EDGE,"98761a0e-d686-4a46-9134-fa1f6f4434ea.filletArc"),sQuery(id+"F0.wireOp",EDGE,"828cccf2-c6bf-4f99-963a-41c4c980739f.filletArc"),sQuery(id+"F0.wireOp",EDGE,"103ca256-2ef9-437d-bf9e-3dfbfe53d8ef.filletArc"),sQuery(id+"F0.wireOp",EDGE,"ed541100-cfe0-4745-a776-ba2087af7cae.filletArc"),sQuery(id+"F0.wireOp",EDGE,"bcec124a-270f-4962-9b0e-bfe1ee30ba45.filletArc"),sQuery(id+"F0.wireOp",EDGE,"ffb815b5-0439-4a1d-8740-96b920259a73.filletArc")])],"isStart":false})],"blendedInto":[makeQuery(id+"F1.opExtrude","CAP_FACE",FACE,{"disambiguationData":[OSD([sQuery(id+"F0.wireOp",EDGE,"E0"),sQuery(id+"F0.wireOp",EDGE,"E1"),subQ1,subQ0,sQuery(id+"F0.wireOp",EDGE,"E4"),sQuery(id+"F0.wireOp",EDGE,"E5"),sQuery(id+"F0.wireOp",EDGE,"E6"),sQuery(id+"F0.wireOp",EDGE,"E7"),sQuery(id+"F0.wireOp",EDGE,"E8"),sQuery(id+"F0.wireOp",EDGE,"E9"),sQuery(id+"F0.wireOp",EDGE,"E10"),sQuery(id+"F0.wireOp",EDGE,"E11"),sQuery(id+"F0.wireOp",EDGE,"E12"),sQuery(id+"F0.wireOp",EDGE,"E13"),sQuery(id+"F0.wireOp",EDGE,"eY3Ntxxg-AOvC-6Sjp-1Sg7-Dh78Z1ENxIpH"),sQuery(id+"F0.wireOp",EDGE,"MyhiPNTX-cIqE-LlnS-pzt5-9fsmOIbbkCBx"),sQuery(id+"F0.wireOp",EDGE,"c5fDbUR1-X0vD-gyia-IhE2-5vfisiyByv1Z"),sQuery(id+"F0.wireOp",EDGE,"z3w7DU23-CNS4-8nrn-3kLT-20PgSTqFnzF7"),sQuery(id+"F0.wireOp",EDGE,"hVG7QURc-v0VO-WvcA-oFbQ-66XRPdHWUu1N"),sQuery(id+"F0.wireOp",EDGE,"sfXvGUbo-ry80-gNXO-uOhN-L8BNUFceVqag"),sQuery(id+"F0.wireOp",EDGE,"QFO76mAv-pKme-nUwV-aMAa-C3MPOYOEvzGl"),sQuery(id+"F0.wireOp",EDGE,"fpymSL76-tXuZ-IzAU-FBSV-KsOygqMtrIGQ"),sQuery(id+"F0.wireOp",EDGE,"9a1d0dfd-7d57-477c-bff2-5a3fdc463cc7.filletArc"),sQuery(id+"F0.wireOp",EDGE,"38622195-8d8f-4664-a9bd-1ddf4e6b9831.filletArc"),sQuery(id+"F0.wireOp",EDGE,"98761a0e-d686-4a46-9134-fa1f6f4434ea.filletArc"),sQuery(id+"F0.wireOp",EDGE,"828cccf2-c6bf-4f99-963a-41c4c980739f.filletArc"),sQuery(id+"F0.wireOp",EDGE,"103ca256-2ef9-437d-bf9e-3dfbfe53d8ef.filletArc"),sQuery(id+"F0.wireOp",EDGE,"ed541100-cfe0-4745-a776-ba2087af7cae.filletArc"),sQuery(id+"F0.wireOp",EDGE,"bcec124a-270f-4962-9b0e-bfe1ee30ba45.filletArc"),sQuery(id+"F0.wireOp",EDGE,"ffb815b5-0439-4a1d-8740-96b920259a73.filletArc")])],"isStart":false})]}),makeQuery(id+"F17.opFillet","BLEND_FACE",FACE,{"disambiguationData":[OSD([subQ1,subQ0])]})],"blendedInto":[makeQuery(id+"F17.opFillet","BLEND_FACE",FACE,{"disambiguationData":[OSD([subQ1,subQ0])]})]});}
            var Q1;
            {var subQ0=sQuery(id+"F0.wireOp",EDGE,"E5");var subQ1=sQuery(id+"F0.wireOp",EDGE,"E4");Q1=makeQuery(id+"F19.opChamfer","BLEND_EDGE",EDGE,{"blendedFrom":[makeQuery(id+"F18.opFillet","BLEND_EDGE",EDGE,{"blendedFrom":[makeQuery(id+"F1.opExtrude","SWEPT_EDGE",EDGE,{"disambiguationData":[OSD([subQ1,subQ0])]}),makeQuery(id+"F1.opExtrude","CAP_FACE",FACE,{"disambiguationData":[OSD([sQuery(id+"F0.wireOp",EDGE,"E0"),sQuery(id+"F0.wireOp",EDGE,"E1"),sQuery(id+"F0.wireOp",EDGE,"E2"),sQuery(id+"F0.wireOp",EDGE,"E3"),subQ1,subQ0,sQuery(id+"F0.wireOp",EDGE,"E6"),sQuery(id+"F0.wireOp",EDGE,"E7"),sQuery(id+"F0.wireOp",EDGE,"E8"),sQuery(id+"F0.wireOp",EDGE,"E9"),sQuery(id+"F0.wireOp",EDGE,"E10"),sQuery(id+"F0.wireOp",EDGE,"E11"),sQuery(id+"F0.wireOp",EDGE,"E12"),sQuery(id+"F0.wireOp",EDGE,"E13"),sQuery(id+"F0.wireOp",EDGE,"eY3Ntxxg-AOvC-6Sjp-1Sg7-Dh78Z1ENxIpH"),sQuery(id+"F0.wireOp",EDGE,"MyhiPNTX-cIqE-LlnS-pzt5-9fsmOIbbkCBx"),sQuery(id+"F0.wireOp",EDGE,"c5fDbUR1-X0vD-gyia-IhE2-5vfisiyByv1Z"),sQuery(id+"F0.wireOp",EDGE,"z3w7DU23-CNS4-8nrn-3kLT-20PgSTqFnzF7"),sQuery(id+"F0.wireOp",EDGE,"hVG7QURc-v0VO-WvcA-oFbQ-66XRPdHWUu1N"),sQuery(id+"F0.wireOp",EDGE,"sfXvGUbo-ry80-gNXO-uOhN-L8BNUFceVqag"),sQuery(id+"F0.wireOp",EDGE,"QFO76mAv-pKme-nUwV-aMAa-C3MPOYOEvzGl"),sQuery(id+"F0.wireOp",EDGE,"fpymSL76-tXuZ-IzAU-FBSV-KsOygqMtrIGQ"),sQuery(id+"F0.wireOp",EDGE,"9a1d0dfd-7d57-477c-bff2-5a3fdc463cc7.filletArc"),sQuery(id+"F0.wireOp",EDGE,"38622195-8d8f-4664-a9bd-1ddf4e6b9831.filletArc"),sQuery(id+"F0.wireOp",EDGE,"98761a0e-d686-4a46-9134-fa1f6f4434ea.filletArc"),sQuery(id+"F0.wireOp",EDGE,"828cccf2-c6bf-4f99-963a-41c4c980739f.filletArc"),sQuery(id+"F0.wireOp",EDGE,"103ca256-2ef9-437d-bf9e-3dfbfe53d8ef.filletArc"),sQuery(id+"F0.wireOp",EDGE,"ed541100-cfe0-4745-a776-ba2087af7cae.filletArc"),sQuery(id+"F0.wireOp",EDGE,"bcec124a-270f-4962-9b0e-bfe1ee30ba45.filletArc"),sQuery(id+"F0.wireOp",EDGE,"ffb815b5-0439-4a1d-8740-96b920259a73.filletArc")])],"isStart":false})],"blendedInto":[makeQuery(id+"F1.opExtrude","CAP_FACE",FACE,{"disambiguationData":[OSD([sQuery(id+"F0.wireOp",EDGE,"E0"),sQuery(id+"F0.wireOp",EDGE,"E1"),sQuery(id+"F0.wireOp",EDGE,"E2"),sQuery(id+"F0.wireOp",EDGE,"E3"),subQ1,subQ0,sQuery(id+"F0.wireOp",EDGE,"E6"),sQuery(id+"F0.wireOp",EDGE,"E7"),sQuery(id+"F0.wireOp",EDGE,"E8"),sQuery(id+"F0.wireOp",EDGE,"E9"),sQuery(id+"F0.wireOp",EDGE,"E10"),sQuery(id+"F0.wireOp",EDGE,"E11"),sQuery(id+"F0.wireOp",EDGE,"E12"),sQuery(id+"F0.wireOp",EDGE,"E13"),sQuery(id+"F0.wireOp",EDGE,"eY3Ntxxg-AOvC-6Sjp-1Sg7-Dh78Z1ENxIpH"),sQuery(id+"F0.wireOp",EDGE,"MyhiPNTX-cIqE-LlnS-pzt5-9fsmOIbbkCBx"),sQuery(id+"F0.wireOp",EDGE,"c5fDbUR1-X0vD-gyia-IhE2-5vfisiyByv1Z"),sQuery(id+"F0.wireOp",EDGE,"z3w7DU23-CNS4-8nrn-3kLT-20PgSTqFnzF7"),sQuery(id+"F0.wireOp",EDGE,"hVG7QURc-v0VO-WvcA-oFbQ-66XRPdHWUu1N"),sQuery(id+"F0.wireOp",EDGE,"sfXvGUbo-ry80-gNXO-uOhN-L8BNUFceVqag"),sQuery(id+"F0.wireOp",EDGE,"QFO76mAv-pKme-nUwV-aMAa-C3MPOYOEvzGl"),sQuery(id+"F0.wireOp",EDGE,"fpymSL76-tXuZ-IzAU-FBSV-KsOygqMtrIGQ"),sQuery(id+"F0.wireOp",EDGE,"9a1d0dfd-7d57-477c-bff2-5a3fdc463cc7.filletArc"),sQuery(id+"F0.wireOp",EDGE,"38622195-8d8f-4664-a9bd-1ddf4e6b9831.filletArc"),sQuery(id+"F0.wireOp",EDGE,"98761a0e-d686-4a46-9134-fa1f6f4434ea.filletArc"),sQuery(id+"F0.wireOp",EDGE,"828cccf2-c6bf-4f99-963a-41c4c980739f.filletArc"),sQuery(id+"F0.wireOp",EDGE,"103ca256-2ef9-437d-bf9e-3dfbfe53d8ef.filletArc"),sQuery(id+"F0.wireOp",EDGE,"ed541100-cfe0-4745-a776-ba2087af7cae.filletArc"),sQuery(id+"F0.wireOp",EDGE,"bcec124a-270f-4962-9b0e-bfe1ee30ba45.filletArc"),sQuery(id+"F0.wireOp",EDGE,"ffb815b5-0439-4a1d-8740-96b920259a73.filletArc")])],"isStart":false})]}),makeQuery(id+"F18.opFillet","BLEND_FACE",FACE,{"disambiguationData":[OSD([subQ1,subQ0])]})],"blendedInto":[makeQuery(id+"F18.opFillet","BLEND_FACE",FACE,{"disambiguationData":[OSD([subQ1,subQ0])]})]});}
            var Q2;
            {var subQ0=sQuery(id+"F0.wireOp",EDGE,"E9");var subQ1=sQuery(id+"F0.wireOp",EDGE,"E8");Q2=makeQuery(id+"F19.opChamfer","BLEND_EDGE",EDGE,{"blendedFrom":[makeQuery(id+"F18.opFillet","BLEND_EDGE",EDGE,{"blendedFrom":[makeQuery(id+"F1.opExtrude","SWEPT_EDGE",EDGE,{"disambiguationData":[OSD([subQ1,subQ0])]}),makeQuery(id+"F1.opExtrude","CAP_FACE",FACE,{"disambiguationData":[OSD([sQuery(id+"F0.wireOp",EDGE,"E0"),sQuery(id+"F0.wireOp",EDGE,"E1"),sQuery(id+"F0.wireOp",EDGE,"E2"),sQuery(id+"F0.wireOp",EDGE,"E3"),sQuery(id+"F0.wireOp",EDGE,"E4"),sQuery(id+"F0.wireOp",EDGE,"E5"),sQuery(id+"F0.wireOp",EDGE,"E6"),sQuery(id+"F0.wireOp",EDGE,"E7"),subQ1,subQ0,sQuery(id+"F0.wireOp",EDGE,"E10"),sQuery(id+"F0.wireOp",EDGE,"E11"),sQuery(id+"F0.wireOp",EDGE,"E12"),sQuery(id+"F0.wireOp",EDGE,"E13"),sQuery(id+"F0.wireOp",EDGE,"eY3Ntxxg-AOvC-6Sjp-1Sg7-Dh78Z1ENxIpH"),sQuery(id+"F0.wireOp",EDGE,"MyhiPNTX-cIqE-LlnS-pzt5-9fsmOIbbkCBx"),sQuery(id+"F0.wireOp",EDGE,"c5fDbUR1-X0vD-gyia-IhE2-5vfisiyByv1Z"),sQuery(id+"F0.wireOp",EDGE,"z3w7DU23-CNS4-8nrn-3kLT-20PgSTqFnzF7"),sQuery(id+"F0.wireOp",EDGE,"hVG7QURc-v0VO-WvcA-oFbQ-66XRPdHWUu1N"),sQuery(id+"F0.wireOp",EDGE,"sfXvGUbo-ry80-gNXO-uOhN-L8BNUFceVqag"),sQuery(id+"F0.wireOp",EDGE,"QFO76mAv-pKme-nUwV-aMAa-C3MPOYOEvzGl"),sQuery(id+"F0.wireOp",EDGE,"fpymSL76-tXuZ-IzAU-FBSV-KsOygqMtrIGQ"),sQuery(id+"F0.wireOp",EDGE,"9a1d0dfd-7d57-477c-bff2-5a3fdc463cc7.filletArc"),sQuery(id+"F0.wireOp",EDGE,"38622195-8d8f-4664-a9bd-1ddf4e6b9831.filletArc"),sQuery(id+"F0.wireOp",EDGE,"98761a0e-d686-4a46-9134-fa1f6f4434ea.filletArc"),sQuery(id+"F0.wireOp",EDGE,"828cccf2-c6bf-4f99-963a-41c4c980739f.filletArc"),sQuery(id+"F0.wireOp",EDGE,"103ca256-2ef9-437d-bf9e-3dfbfe53d8ef.filletArc"),sQuery(id+"F0.wireOp",EDGE,"ed541100-cfe0-4745-a776-ba2087af7cae.filletArc"),sQuery(id+"F0.wireOp",EDGE,"bcec124a-270f-4962-9b0e-bfe1ee30ba45.filletArc"),sQuery(id+"F0.wireOp",EDGE,"ffb815b5-0439-4a1d-8740-96b920259a73.filletArc")])],"isStart":false})],"blendedInto":[makeQuery(id+"F1.opExtrude","CAP_FACE",FACE,{"disambiguationData":[OSD([sQuery(id+"F0.wireOp",EDGE,"E0"),sQuery(id+"F0.wireOp",EDGE,"E1"),sQuery(id+"F0.wireOp",EDGE,"E2"),sQuery(id+"F0.wireOp",EDGE,"E3"),sQuery(id+"F0.wireOp",EDGE,"E4"),sQuery(id+"F0.wireOp",EDGE,"E5"),sQuery(id+"F0.wireOp",EDGE,"E6"),sQuery(id+"F0.wireOp",EDGE,"E7"),subQ1,subQ0,sQuery(id+"F0.wireOp",EDGE,"E10"),sQuery(id+"F0.wireOp",EDGE,"E11"),sQuery(id+"F0.wireOp",EDGE,"E12"),sQuery(id+"F0.wireOp",EDGE,"E13"),sQuery(id+"F0.wireOp",EDGE,"eY3Ntxxg-AOvC-6Sjp-1Sg7-Dh78Z1ENxIpH"),sQuery(id+"F0.wireOp",EDGE,"MyhiPNTX-cIqE-LlnS-pzt5-9fsmOIbbkCBx"),sQuery(id+"F0.wireOp",EDGE,"c5fDbUR1-X0vD-gyia-IhE2-5vfisiyByv1Z"),sQuery(id+"F0.wireOp",EDGE,"z3w7DU23-CNS4-8nrn-3kLT-20PgSTqFnzF7"),sQuery(id+"F0.wireOp",EDGE,"hVG7QURc-v0VO-WvcA-oFbQ-66XRPdHWUu1N"),sQuery(id+"F0.wireOp",EDGE,"sfXvGUbo-ry80-gNXO-uOhN-L8BNUFceVqag"),sQuery(id+"F0.wireOp",EDGE,"QFO76mAv-pKme-nUwV-aMAa-C3MPOYOEvzGl"),sQuery(id+"F0.wireOp",EDGE,"fpymSL76-tXuZ-IzAU-FBSV-KsOygqMtrIGQ"),sQuery(id+"F0.wireOp",EDGE,"9a1d0dfd-7d57-477c-bff2-5a3fdc463cc7.filletArc"),sQuery(id+"F0.wireOp",EDGE,"38622195-8d8f-4664-a9bd-1ddf4e6b9831.filletArc"),sQuery(id+"F0.wireOp",EDGE,"98761a0e-d686-4a46-9134-fa1f6f4434ea.filletArc"),sQuery(id+"F0.wireOp",EDGE,"828cccf2-c6bf-4f99-963a-41c4c980739f.filletArc"),sQuery(id+"F0.wireOp",EDGE,"103ca256-2ef9-437d-bf9e-3dfbfe53d8ef.filletArc"),sQuery(id+"F0.wireOp",EDGE,"ed541100-cfe0-4745-a776-ba2087af7cae.filletArc"),sQuery(id+"F0.wireOp",EDGE,"bcec124a-270f-4962-9b0e-bfe1ee30ba45.filletArc"),sQuery(id+"F0.wireOp",EDGE,"ffb815b5-0439-4a1d-8740-96b920259a73.filletArc")])],"isStart":false})]}),makeQuery(id+"F18.opFillet","BLEND_FACE",FACE,{"disambiguationData":[OSD([subQ1,subQ0])]})],"blendedInto":[makeQuery(id+"F18.opFillet","BLEND_FACE",FACE,{"disambiguationData":[OSD([subQ1,subQ0])]})]});}
            var Q3;
            {var subQ0=sQuery(id+"F0.wireOp",EDGE,"E1");var subQ1=sQuery(id+"F0.wireOp",EDGE,"E0");Q3=makeQuery(id+"F19.opChamfer","BLEND_EDGE",EDGE,{"blendedFrom":[makeQuery(id+"F17.opFillet","BLEND_EDGE",EDGE,{"blendedFrom":[makeQuery(id+"F1.opExtrude","SWEPT_EDGE",EDGE,{"disambiguationData":[OSD([subQ1,subQ0])]}),makeQuery(id+"F1.opExtrude","CAP_FACE",FACE,{"disambiguationData":[OSD([subQ1,subQ0,sQuery(id+"F0.wireOp",EDGE,"E2"),sQuery(id+"F0.wireOp",EDGE,"E3"),sQuery(id+"F0.wireOp",EDGE,"E4"),sQuery(id+"F0.wireOp",EDGE,"E5"),sQuery(id+"F0.wireOp",EDGE,"E6"),sQuery(id+"F0.wireOp",EDGE,"E7"),sQuery(id+"F0.wireOp",EDGE,"E8"),sQuery(id+"F0.wireOp",EDGE,"E9"),sQuery(id+"F0.wireOp",EDGE,"E10"),sQuery(id+"F0.wireOp",EDGE,"E11"),sQuery(id+"F0.wireOp",EDGE,"E12"),sQuery(id+"F0.wireOp",EDGE,"E13"),sQuery(id+"F0.wireOp",EDGE,"eY3Ntxxg-AOvC-6Sjp-1Sg7-Dh78Z1ENxIpH"),sQuery(id+"F0.wireOp",EDGE,"MyhiPNTX-cIqE-LlnS-pzt5-9fsmOIbbkCBx"),sQuery(id+"F0.wireOp",EDGE,"c5fDbUR1-X0vD-gyia-IhE2-5vfisiyByv1Z"),sQuery(id+"F0.wireOp",EDGE,"z3w7DU23-CNS4-8nrn-3kLT-20PgSTqFnzF7"),sQuery(id+"F0.wireOp",EDGE,"hVG7QURc-v0VO-WvcA-oFbQ-66XRPdHWUu1N"),sQuery(id+"F0.wireOp",EDGE,"sfXvGUbo-ry80-gNXO-uOhN-L8BNUFceVqag"),sQuery(id+"F0.wireOp",EDGE,"QFO76mAv-pKme-nUwV-aMAa-C3MPOYOEvzGl"),sQuery(id+"F0.wireOp",EDGE,"fpymSL76-tXuZ-IzAU-FBSV-KsOygqMtrIGQ"),sQuery(id+"F0.wireOp",EDGE,"9a1d0dfd-7d57-477c-bff2-5a3fdc463cc7.filletArc"),sQuery(id+"F0.wireOp",EDGE,"38622195-8d8f-4664-a9bd-1ddf4e6b9831.filletArc"),sQuery(id+"F0.wireOp",EDGE,"98761a0e-d686-4a46-9134-fa1f6f4434ea.filletArc"),sQuery(id+"F0.wireOp",EDGE,"828cccf2-c6bf-4f99-963a-41c4c980739f.filletArc"),sQuery(id+"F0.wireOp",EDGE,"103ca256-2ef9-437d-bf9e-3dfbfe53d8ef.filletArc"),sQuery(id+"F0.wireOp",EDGE,"ed541100-cfe0-4745-a776-ba2087af7cae.filletArc"),sQuery(id+"F0.wireOp",EDGE,"bcec124a-270f-4962-9b0e-bfe1ee30ba45.filletArc"),sQuery(id+"F0.wireOp",EDGE,"ffb815b5-0439-4a1d-8740-96b920259a73.filletArc")])],"isStart":false})],"blendedInto":[makeQuery(id+"F1.opExtrude","CAP_FACE",FACE,{"disambiguationData":[OSD([subQ1,subQ0,sQuery(id+"F0.wireOp",EDGE,"E2"),sQuery(id+"F0.wireOp",EDGE,"E3"),sQuery(id+"F0.wireOp",EDGE,"E4"),sQuery(id+"F0.wireOp",EDGE,"E5"),sQuery(id+"F0.wireOp",EDGE,"E6"),sQuery(id+"F0.wireOp",EDGE,"E7"),sQuery(id+"F0.wireOp",EDGE,"E8"),sQuery(id+"F0.wireOp",EDGE,"E9"),sQuery(id+"F0.wireOp",EDGE,"E10"),sQuery(id+"F0.wireOp",EDGE,"E11"),sQuery(id+"F0.wireOp",EDGE,"E12"),sQuery(id+"F0.wireOp",EDGE,"E13"),sQuery(id+"F0.wireOp",EDGE,"eY3Ntxxg-AOvC-6Sjp-1Sg7-Dh78Z1ENxIpH"),sQuery(id+"F0.wireOp",EDGE,"MyhiPNTX-cIqE-LlnS-pzt5-9fsmOIbbkCBx"),sQuery(id+"F0.wireOp",EDGE,"c5fDbUR1-X0vD-gyia-IhE2-5vfisiyByv1Z"),sQuery(id+"F0.wireOp",EDGE,"z3w7DU23-CNS4-8nrn-3kLT-20PgSTqFnzF7"),sQuery(id+"F0.wireOp",EDGE,"hVG7QURc-v0VO-WvcA-oFbQ-66XRPdHWUu1N"),sQuery(id+"F0.wireOp",EDGE,"sfXvGUbo-ry80-gNXO-uOhN-L8BNUFceVqag"),sQuery(id+"F0.wireOp",EDGE,"QFO76mAv-pKme-nUwV-aMAa-C3MPOYOEvzGl"),sQuery(id+"F0.wireOp",EDGE,"fpymSL76-tXuZ-IzAU-FBSV-KsOygqMtrIGQ"),sQuery(id+"F0.wireOp",EDGE,"9a1d0dfd-7d57-477c-bff2-5a3fdc463cc7.filletArc"),sQuery(id+"F0.wireOp",EDGE,"38622195-8d8f-4664-a9bd-1ddf4e6b9831.filletArc"),sQuery(id+"F0.wireOp",EDGE,"98761a0e-d686-4a46-9134-fa1f6f4434ea.filletArc"),sQuery(id+"F0.wireOp",EDGE,"828cccf2-c6bf-4f99-963a-41c4c980739f.filletArc"),sQuery(id+"F0.wireOp",EDGE,"103ca256-2ef9-437d-bf9e-3dfbfe53d8ef.filletArc"),sQuery(id+"F0.wireOp",EDGE,"ed541100-cfe0-4745-a776-ba2087af7cae.filletArc"),sQuery(id+"F0.wireOp",EDGE,"bcec124a-270f-4962-9b0e-bfe1ee30ba45.filletArc"),sQuery(id+"F0.wireOp",EDGE,"ffb815b5-0439-4a1d-8740-96b920259a73.filletArc")])],"isStart":false})]}),makeQuery(id+"F17.opFillet","BLEND_FACE",FACE,{"disambiguationData":[OSD([subQ1,subQ0])]})],"blendedInto":[makeQuery(id+"F17.opFillet","BLEND_FACE",FACE,{"disambiguationData":[OSD([subQ1,subQ0])]})]});}
            var Q4;
            {var subQ0=sQuery(id+"F0.wireOp",EDGE,"E1");var subQ1=sQuery(id+"F0.wireOp",EDGE,"E0");Q4=makeQuery(id+"F17.opFillet","BLEND_EDGE",EDGE,{"blendedFrom":[makeQuery(id+"F1.opExtrude","SWEPT_EDGE",EDGE,{"disambiguationData":[OSD([subQ1,subQ0])]}),makeQuery(id+"F1.opExtrude","CAP_FACE",FACE,{"disambiguationData":[OSD([subQ1,subQ0,sQuery(id+"F0.wireOp",EDGE,"E2"),sQuery(id+"F0.wireOp",EDGE,"E3"),sQuery(id+"F0.wireOp",EDGE,"E4"),sQuery(id+"F0.wireOp",EDGE,"E5"),sQuery(id+"F0.wireOp",EDGE,"E6"),sQuery(id+"F0.wireOp",EDGE,"E7"),sQuery(id+"F0.wireOp",EDGE,"E8"),sQuery(id+"F0.wireOp",EDGE,"E9"),sQuery(id+"F0.wireOp",EDGE,"E10"),sQuery(id+"F0.wireOp",EDGE,"E11"),sQuery(id+"F0.wireOp",EDGE,"E12"),sQuery(id+"F0.wireOp",EDGE,"E13"),sQuery(id+"F0.wireOp",EDGE,"Ze1lcFJT-wXSP-p6Sp-ibzG-PLGItWCrLXdm"),sQuery(id+"F0.wireOp",EDGE,"LCGSbrbs-ELcM-2btd-Nxrq-0X5GcQ4YE41g"),sQuery(id+"F0.wireOp",EDGE,"LftxxQDg-wbQU-W9M1-Aj5u-4wwMhXT5RF4g"),sQuery(id+"F0.wireOp",EDGE,"TYH3NWJP-SDMf-QQyj-lhjL-s3Mkt6MxWAxo")])],"isStart":true})],"blendedInto":[makeQuery(id+"F1.opExtrude","CAP_FACE",FACE,{"disambiguationData":[OSD([subQ1,subQ0,sQuery(id+"F0.wireOp",EDGE,"E2"),sQuery(id+"F0.wireOp",EDGE,"E3"),sQuery(id+"F0.wireOp",EDGE,"E4"),sQuery(id+"F0.wireOp",EDGE,"E5"),sQuery(id+"F0.wireOp",EDGE,"E6"),sQuery(id+"F0.wireOp",EDGE,"E7"),sQuery(id+"F0.wireOp",EDGE,"E8"),sQuery(id+"F0.wireOp",EDGE,"E9"),sQuery(id+"F0.wireOp",EDGE,"E10"),sQuery(id+"F0.wireOp",EDGE,"E11"),sQuery(id+"F0.wireOp",EDGE,"E12"),sQuery(id+"F0.wireOp",EDGE,"E13"),sQuery(id+"F0.wireOp",EDGE,"Ze1lcFJT-wXSP-p6Sp-ibzG-PLGItWCrLXdm"),sQuery(id+"F0.wireOp",EDGE,"LCGSbrbs-ELcM-2btd-Nxrq-0X5GcQ4YE41g"),sQuery(id+"F0.wireOp",EDGE,"LftxxQDg-wbQU-W9M1-Aj5u-4wwMhXT5RF4g"),sQuery(id+"F0.wireOp",EDGE,"TYH3NWJP-SDMf-QQyj-lhjL-s3Mkt6MxWAxo")])],"isStart":true})]});}
            var Q5;
            Q5=makeQuery(id+"F1.opExtrude","CAP_EDGE",EDGE,{"disambiguationData":[OSD([sQuery(id+"F0.wireOp",EDGE,"E8")])],"isStart":true});
            var Q6;
            Q6=makeQuery(id+"F1.opExtrude","CAP_EDGE",EDGE,{"disambiguationData":[OSD([sQuery(id+"F0.wireOp",EDGE,"E5")])],"isStart":true});
            var Q7;
            {var subQ0=sQuery(id+"F0.wireOp",EDGE,"E3");var subQ1=sQuery(id+"F0.wireOp",EDGE,"E2");Q7=makeQuery(id+"F17.opFillet","BLEND_EDGE",EDGE,{"blendedFrom":[makeQuery(id+"F1.opExtrude","SWEPT_EDGE",EDGE,{"disambiguationData":[OSD([subQ1,subQ0])]}),makeQuery(id+"F1.opExtrude","CAP_FACE",FACE,{"disambiguationData":[OSD([sQuery(id+"F0.wireOp",EDGE,"E0"),sQuery(id+"F0.wireOp",EDGE,"E1"),subQ1,subQ0,sQuery(id+"F0.wireOp",EDGE,"E4"),sQuery(id+"F0.wireOp",EDGE,"E5"),sQuery(id+"F0.wireOp",EDGE,"E6"),sQuery(id+"F0.wireOp",EDGE,"E7"),sQuery(id+"F0.wireOp",EDGE,"E8"),sQuery(id+"F0.wireOp",EDGE,"E9"),sQuery(id+"F0.wireOp",EDGE,"E10"),sQuery(id+"F0.wireOp",EDGE,"E11"),sQuery(id+"F0.wireOp",EDGE,"E12"),sQuery(id+"F0.wireOp",EDGE,"E13"),sQuery(id+"F0.wireOp",EDGE,"Ze1lcFJT-wXSP-p6Sp-ibzG-PLGItWCrLXdm"),sQuery(id+"F0.wireOp",EDGE,"LCGSbrbs-ELcM-2btd-Nxrq-0X5GcQ4YE41g"),sQuery(id+"F0.wireOp",EDGE,"LftxxQDg-wbQU-W9M1-Aj5u-4wwMhXT5RF4g"),sQuery(id+"F0.wireOp",EDGE,"TYH3NWJP-SDMf-QQyj-lhjL-s3Mkt6MxWAxo")])],"isStart":true})],"blendedInto":[makeQuery(id+"F1.opExtrude","CAP_FACE",FACE,{"disambiguationData":[OSD([sQuery(id+"F0.wireOp",EDGE,"E0"),sQuery(id+"F0.wireOp",EDGE,"E1"),subQ1,subQ0,sQuery(id+"F0.wireOp",EDGE,"E4"),sQuery(id+"F0.wireOp",EDGE,"E5"),sQuery(id+"F0.wireOp",EDGE,"E6"),sQuery(id+"F0.wireOp",EDGE,"E7"),sQuery(id+"F0.wireOp",EDGE,"E8"),sQuery(id+"F0.wireOp",EDGE,"E9"),sQuery(id+"F0.wireOp",EDGE,"E10"),sQuery(id+"F0.wireOp",EDGE,"E11"),sQuery(id+"F0.wireOp",EDGE,"E12"),sQuery(id+"F0.wireOp",EDGE,"E13"),sQuery(id+"F0.wireOp",EDGE,"Ze1lcFJT-wXSP-p6Sp-ibzG-PLGItWCrLXdm"),sQuery(id+"F0.wireOp",EDGE,"LCGSbrbs-ELcM-2btd-Nxrq-0X5GcQ4YE41g"),sQuery(id+"F0.wireOp",EDGE,"LftxxQDg-wbQU-W9M1-Aj5u-4wwMhXT5RF4g"),sQuery(id+"F0.wireOp",EDGE,"TYH3NWJP-SDMf-QQyj-lhjL-s3Mkt6MxWAxo")])],"isStart":true})]});}
            var Q8;
            Q8=makeQuery(id+"F11.boolean.opBoolean","COPY",FACE,{"derivedFrom":makeQuery(id+"F11.opExtrude","SWEPT_FACE",FACE,{"disambiguationData":[OSD([sQuery(id+"F10.wireOp",EDGE,"E71")])]})});
            var Q9;
            Q9=makeQuery(id+"F11.boolean.opBoolean","COPY",FACE,{"derivedFrom":makeQuery(id+"F11.opExtrude","SWEPT_FACE",FACE,{"disambiguationData":[OSD([sQuery(id+"F10.wireOp",EDGE,"E70")])]})});
            var Q10;
            Q10=makeQuery(id+"F11.boolean.opBoolean","COPY",FACE,{"derivedFrom":makeQuery(id+"F11.opExtrude","SWEPT_FACE",FACE,{"disambiguationData":[OSD([sQuery(id+"F10.wireOp",EDGE,"E68")])]})});
            var Q11;
            Q11=makeQuery(id+"F11.boolean.opBoolean","COPY",FACE,{"derivedFrom":makeQuery(id+"F11.opExtrude","SWEPT_FACE",FACE,{"disambiguationData":[OSD([sQuery(id+"F10.wireOp",EDGE,"E69")])]})});
            var Q12;
            Q12=makeQuery(id+"F9.boolean.opBoolean","COPY",FACE,{"derivedFrom":makeQuery(id+"F9.opExtrude","SWEPT_FACE",FACE,{"disambiguationData":[OSD([sQuery(id+"F8.wireOp",EDGE,"E56.MirrorC")])]})});
            var Q13;
            Q13=makeQuery(id+"F9.boolean.opBoolean","COPY",FACE,{"derivedFrom":makeQuery(id+"F9.opExtrude","SWEPT_FACE",FACE,{"disambiguationData":[OSD([sQuery(id+"F8.wireOp",EDGE,"E58.MirrorC")])]})});
            var Q14;
            Q14=makeQuery(id+"F9.boolean.opBoolean","COPY",FACE,{"derivedFrom":makeQuery(id+"F9.opExtrude","SWEPT_FACE",FACE,{"disambiguationData":[OSD([sQuery(id+"F8.wireOp",EDGE,"E57.MirrorC")])]})});
            var Q15;
            Q15=makeQuery(id+"F9.boolean.opBoolean","COPY",FACE,{"derivedFrom":makeQuery(id+"F9.opExtrude","SWEPT_FACE",FACE,{"disambiguationData":[OSD([sQuery(id+"F8.wireOp",EDGE,"E62.MirrorC")])]})});
            var Q16;
            Q16=makeQuery(id+"F9.boolean.opBoolean","COPY",FACE,{"derivedFrom":makeQuery(id+"F9.opExtrude","SWEPT_FACE",FACE,{"disambiguationData":[OSD([sQuery(id+"F8.wireOp",EDGE,"E63.MirrorC")])]})});
            var Q17;
            Q17=makeQuery(id+"F9.boolean.opBoolean","COPY",FACE,{"derivedFrom":makeQuery(id+"F9.opExtrude","SWEPT_FACE",FACE,{"disambiguationData":[OSD([sQuery(id+"F8.wireOp",EDGE,"E65.MirrorC")])]})});
            var Q18;
            Q18=makeQuery(id+"F9.boolean.opBoolean","COPY",FACE,{"derivedFrom":makeQuery(id+"F9.opExtrude","SWEPT_FACE",FACE,{"disambiguationData":[OSD([sQuery(id+"F8.wireOp",EDGE,"E64.MirrorC")])]})});
            var Q19;
            Q19=makeQuery(id+"F9.boolean.opBoolean","COPY",FACE,{"derivedFrom":makeQuery(id+"F9.opExtrude","SWEPT_FACE",FACE,{"disambiguationData":[OSD([sQuery(id+"F8.wireOp",EDGE,"E60.MirrorC")])]})});
            var Q20;
            Q20=makeQuery(id+"F9.boolean.opBoolean","COPY",FACE,{"derivedFrom":makeQuery(id+"F9.opExtrude","SWEPT_FACE",FACE,{"disambiguationData":[OSD([sQuery(id+"F8.wireOp",EDGE,"E61.MirrorC")])]})});
            var Q21;
            Q21=makeQuery(id+"F9.boolean.opBoolean","COPY",FACE,{"derivedFrom":makeQuery(id+"F9.opExtrude","SWEPT_FACE",FACE,{"disambiguationData":[OSD([sQuery(id+"F8.wireOp",EDGE,"E54")])]})});
            var Q22;
            Q22=makeQuery(id+"F9.boolean.opBoolean","COPY",FACE,{"derivedFrom":makeQuery(id+"F9.opExtrude","SWEPT_FACE",FACE,{"disambiguationData":[OSD([sQuery(id+"F8.wireOp",EDGE,"E55.1.0")])]})});
            var Q23;
            Q23=makeQuery(id+"F9.boolean.opBoolean","COPY",FACE,{"derivedFrom":makeQuery(id+"F9.opExtrude","SWEPT_FACE",FACE,{"disambiguationData":[OSD([sQuery(id+"F8.wireOp",EDGE,"E55.2.0")])]})});
            var Q24;
            Q24=makeQuery(id+"F13.boolean.opBoolean","COPY",FACE,{"derivedFrom":makeQuery(id+"F13.opExtrude","SWEPT_FACE",FACE,{"disambiguationData":[OSD([sQuery(id+"F12.wireOp",EDGE,"E77")])]})});
            var Q25;
            Q25=makeQuery(id+"F13.boolean.opBoolean","COPY",FACE,{"derivedFrom":makeQuery(id+"F13.opExtrude","SWEPT_FACE",FACE,{"disambiguationData":[OSD([sQuery(id+"F12.wireOp",EDGE,"E78.MirrorC")])]})});
            var Q26;
            Q26=makeQuery(id+"F13.boolean.opBoolean","COPY",FACE,{"derivedFrom":makeQuery(id+"F13.opExtrude","SWEPT_FACE",FACE,{"disambiguationData":[OSD([sQuery(id+"F12.wireOp",EDGE,"E79.MirrorC")])]})});
            var Q27;
            Q27=makeQuery(id+"F13.boolean.opBoolean","COPY",FACE,{"derivedFrom":makeQuery(id+"F13.opExtrude","SWEPT_FACE",FACE,{"disambiguationData":[OSD([sQuery(id+"F12.wireOp",EDGE,"E80.MirrorC")])]})});
            var Q28;
            Q28=makeQuery(id+"F11.boolean.opBoolean","COPY",EDGE,{"derivedFrom":makeQuery(id+"F11.opExtrude","CAP_EDGE",EDGE,{"disambiguationData":[OSD([sQuery(id+"F10.wireOp",EDGE,"E72.bottom")])],"isStart":true})});
            fillet(context, id + "F23", {"entities" : qUnion([Q0, Q1, Q2, Q3, Q4, Q5, Q6, Q7, Q8, Q9, Q10, Q11, Q12, Q13, Q14, Q15, Q16, Q17, Q18, Q19, Q20, Q21, Q22, Q23, Q24, Q25, Q26, Q27, Q28]), "radius" : .5 * mm, "tangentPropagation" : true, "allowEdgeOverflow" : false});
        }
        {
            var Q0;
            {var subQ0=sQuery(id+"F0.wireOp",EDGE,"E1");var subQ1=sQuery(id+"F0.wireOp",EDGE,"E0");var subQ2=makeQuery(id+"F1.opExtrude","CAP_FACE",FACE,{"disambiguationData":[OSD([subQ1,subQ0,sQuery(id+"F0.wireOp",EDGE,"E2"),sQuery(id+"F0.wireOp",EDGE,"E3"),sQuery(id+"F0.wireOp",EDGE,"E4"),sQuery(id+"F0.wireOp",EDGE,"E5"),sQuery(id+"F0.wireOp",EDGE,"E6"),sQuery(id+"F0.wireOp",EDGE,"E7"),sQuery(id+"F0.wireOp",EDGE,"E8"),sQuery(id+"F0.wireOp",EDGE,"E9"),sQuery(id+"F0.wireOp",EDGE,"E10"),sQuery(id+"F0.wireOp",EDGE,"E11"),sQuery(id+"F0.wireOp",EDGE,"E12"),sQuery(id+"F0.wireOp",EDGE,"E13"),sQuery(id+"F0.wireOp",EDGE,"eY3Ntxxg-AOvC-6Sjp-1Sg7-Dh78Z1ENxIpH"),sQuery(id+"F0.wireOp",EDGE,"MyhiPNTX-cIqE-LlnS-pzt5-9fsmOIbbkCBx"),sQuery(id+"F0.wireOp",EDGE,"c5fDbUR1-X0vD-gyia-IhE2-5vfisiyByv1Z"),sQuery(id+"F0.wireOp",EDGE,"z3w7DU23-CNS4-8nrn-3kLT-20PgSTqFnzF7"),sQuery(id+"F0.wireOp",EDGE,"hVG7QURc-v0VO-WvcA-oFbQ-66XRPdHWUu1N"),sQuery(id+"F0.wireOp",EDGE,"sfXvGUbo-ry80-gNXO-uOhN-L8BNUFceVqag"),sQuery(id+"F0.wireOp",EDGE,"QFO76mAv-pKme-nUwV-aMAa-C3MPOYOEvzGl"),sQuery(id+"F0.wireOp",EDGE,"fpymSL76-tXuZ-IzAU-FBSV-KsOygqMtrIGQ"),sQuery(id+"F0.wireOp",EDGE,"9a1d0dfd-7d57-477c-bff2-5a3fdc463cc7.filletArc"),sQuery(id+"F0.wireOp",EDGE,"38622195-8d8f-4664-a9bd-1ddf4e6b9831.filletArc"),sQuery(id+"F0.wireOp",EDGE,"98761a0e-d686-4a46-9134-fa1f6f4434ea.filletArc"),sQuery(id+"F0.wireOp",EDGE,"828cccf2-c6bf-4f99-963a-41c4c980739f.filletArc"),sQuery(id+"F0.wireOp",EDGE,"103ca256-2ef9-437d-bf9e-3dfbfe53d8ef.filletArc"),sQuery(id+"F0.wireOp",EDGE,"ed541100-cfe0-4745-a776-ba2087af7cae.filletArc"),sQuery(id+"F0.wireOp",EDGE,"bcec124a-270f-4962-9b0e-bfe1ee30ba45.filletArc"),sQuery(id+"F0.wireOp",EDGE,"ffb815b5-0439-4a1d-8740-96b920259a73.filletArc")])],"isStart":false});Q0=makeQuery(id+"F19.opChamfer","BLEND_EDGE",EDGE,{"blendedFrom":[makeQuery(id+"F17.opFillet","BLEND_EDGE",EDGE,{"blendedFrom":[makeQuery(id+"F1.opExtrude","SWEPT_EDGE",EDGE,{"disambiguationData":[OSD([subQ1,subQ0])]}),subQ2],"blendedInto":[subQ2]}),subQ2],"blendedInto":[subQ2]});}
            var Q1;
            {var subQ0=sQuery(id+"F0.wireOp",EDGE,"E5");var subQ1=sQuery(id+"F0.wireOp",EDGE,"E4");var subQ2=makeQuery(id+"F1.opExtrude","CAP_FACE",FACE,{"disambiguationData":[OSD([sQuery(id+"F0.wireOp",EDGE,"E0"),sQuery(id+"F0.wireOp",EDGE,"E1"),sQuery(id+"F0.wireOp",EDGE,"E2"),sQuery(id+"F0.wireOp",EDGE,"E3"),subQ1,subQ0,sQuery(id+"F0.wireOp",EDGE,"E6"),sQuery(id+"F0.wireOp",EDGE,"E7"),sQuery(id+"F0.wireOp",EDGE,"E8"),sQuery(id+"F0.wireOp",EDGE,"E9"),sQuery(id+"F0.wireOp",EDGE,"E10"),sQuery(id+"F0.wireOp",EDGE,"E11"),sQuery(id+"F0.wireOp",EDGE,"E12"),sQuery(id+"F0.wireOp",EDGE,"E13"),sQuery(id+"F0.wireOp",EDGE,"eY3Ntxxg-AOvC-6Sjp-1Sg7-Dh78Z1ENxIpH"),sQuery(id+"F0.wireOp",EDGE,"MyhiPNTX-cIqE-LlnS-pzt5-9fsmOIbbkCBx"),sQuery(id+"F0.wireOp",EDGE,"c5fDbUR1-X0vD-gyia-IhE2-5vfisiyByv1Z"),sQuery(id+"F0.wireOp",EDGE,"z3w7DU23-CNS4-8nrn-3kLT-20PgSTqFnzF7"),sQuery(id+"F0.wireOp",EDGE,"hVG7QURc-v0VO-WvcA-oFbQ-66XRPdHWUu1N"),sQuery(id+"F0.wireOp",EDGE,"sfXvGUbo-ry80-gNXO-uOhN-L8BNUFceVqag"),sQuery(id+"F0.wireOp",EDGE,"QFO76mAv-pKme-nUwV-aMAa-C3MPOYOEvzGl"),sQuery(id+"F0.wireOp",EDGE,"fpymSL76-tXuZ-IzAU-FBSV-KsOygqMtrIGQ"),sQuery(id+"F0.wireOp",EDGE,"9a1d0dfd-7d57-477c-bff2-5a3fdc463cc7.filletArc"),sQuery(id+"F0.wireOp",EDGE,"38622195-8d8f-4664-a9bd-1ddf4e6b9831.filletArc"),sQuery(id+"F0.wireOp",EDGE,"98761a0e-d686-4a46-9134-fa1f6f4434ea.filletArc"),sQuery(id+"F0.wireOp",EDGE,"828cccf2-c6bf-4f99-963a-41c4c980739f.filletArc"),sQuery(id+"F0.wireOp",EDGE,"103ca256-2ef9-437d-bf9e-3dfbfe53d8ef.filletArc"),sQuery(id+"F0.wireOp",EDGE,"ed541100-cfe0-4745-a776-ba2087af7cae.filletArc"),sQuery(id+"F0.wireOp",EDGE,"bcec124a-270f-4962-9b0e-bfe1ee30ba45.filletArc"),sQuery(id+"F0.wireOp",EDGE,"ffb815b5-0439-4a1d-8740-96b920259a73.filletArc")])],"isStart":false});Q1=makeQuery(id+"F19.opChamfer","BLEND_EDGE",EDGE,{"blendedFrom":[makeQuery(id+"F18.opFillet","BLEND_EDGE",EDGE,{"blendedFrom":[makeQuery(id+"F1.opExtrude","SWEPT_EDGE",EDGE,{"disambiguationData":[OSD([subQ1,subQ0])]}),subQ2],"blendedInto":[subQ2]}),subQ2],"blendedInto":[subQ2]});}
            var Q2;
            {var subQ0=sQuery(id+"F0.wireOp",EDGE,"E3");var subQ1=sQuery(id+"F0.wireOp",EDGE,"E2");var subQ2=makeQuery(id+"F1.opExtrude","CAP_FACE",FACE,{"disambiguationData":[OSD([sQuery(id+"F0.wireOp",EDGE,"E0"),sQuery(id+"F0.wireOp",EDGE,"E1"),subQ1,subQ0,sQuery(id+"F0.wireOp",EDGE,"E4"),sQuery(id+"F0.wireOp",EDGE,"E5"),sQuery(id+"F0.wireOp",EDGE,"E6"),sQuery(id+"F0.wireOp",EDGE,"E7"),sQuery(id+"F0.wireOp",EDGE,"E8"),sQuery(id+"F0.wireOp",EDGE,"E9"),sQuery(id+"F0.wireOp",EDGE,"E10"),sQuery(id+"F0.wireOp",EDGE,"E11"),sQuery(id+"F0.wireOp",EDGE,"E12"),sQuery(id+"F0.wireOp",EDGE,"E13"),sQuery(id+"F0.wireOp",EDGE,"eY3Ntxxg-AOvC-6Sjp-1Sg7-Dh78Z1ENxIpH"),sQuery(id+"F0.wireOp",EDGE,"MyhiPNTX-cIqE-LlnS-pzt5-9fsmOIbbkCBx"),sQuery(id+"F0.wireOp",EDGE,"c5fDbUR1-X0vD-gyia-IhE2-5vfisiyByv1Z"),sQuery(id+"F0.wireOp",EDGE,"z3w7DU23-CNS4-8nrn-3kLT-20PgSTqFnzF7"),sQuery(id+"F0.wireOp",EDGE,"hVG7QURc-v0VO-WvcA-oFbQ-66XRPdHWUu1N"),sQuery(id+"F0.wireOp",EDGE,"sfXvGUbo-ry80-gNXO-uOhN-L8BNUFceVqag"),sQuery(id+"F0.wireOp",EDGE,"QFO76mAv-pKme-nUwV-aMAa-C3MPOYOEvzGl"),sQuery(id+"F0.wireOp",EDGE,"fpymSL76-tXuZ-IzAU-FBSV-KsOygqMtrIGQ"),sQuery(id+"F0.wireOp",EDGE,"9a1d0dfd-7d57-477c-bff2-5a3fdc463cc7.filletArc"),sQuery(id+"F0.wireOp",EDGE,"38622195-8d8f-4664-a9bd-1ddf4e6b9831.filletArc"),sQuery(id+"F0.wireOp",EDGE,"98761a0e-d686-4a46-9134-fa1f6f4434ea.filletArc"),sQuery(id+"F0.wireOp",EDGE,"828cccf2-c6bf-4f99-963a-41c4c980739f.filletArc"),sQuery(id+"F0.wireOp",EDGE,"103ca256-2ef9-437d-bf9e-3dfbfe53d8ef.filletArc"),sQuery(id+"F0.wireOp",EDGE,"ed541100-cfe0-4745-a776-ba2087af7cae.filletArc"),sQuery(id+"F0.wireOp",EDGE,"bcec124a-270f-4962-9b0e-bfe1ee30ba45.filletArc"),sQuery(id+"F0.wireOp",EDGE,"ffb815b5-0439-4a1d-8740-96b920259a73.filletArc")])],"isStart":false});Q2=makeQuery(id+"F19.opChamfer","BLEND_EDGE",EDGE,{"blendedFrom":[makeQuery(id+"F17.opFillet","BLEND_EDGE",EDGE,{"blendedFrom":[makeQuery(id+"F1.opExtrude","SWEPT_EDGE",EDGE,{"disambiguationData":[OSD([subQ1,subQ0])]}),subQ2],"blendedInto":[subQ2]}),subQ2],"blendedInto":[subQ2]});}
            var Q3;
            {var subQ0=sQuery(id+"F0.wireOp",EDGE,"E8");Q3=makeQuery(id+"F19.opChamfer","BLEND_EDGE",EDGE,{"blendedFrom":[makeQuery(id+"F1.opExtrude","CAP_EDGE",EDGE,{"disambiguationData":[OSD([subQ0])],"isStart":false}),makeQuery(id+"F1.opExtrude","CAP_FACE",FACE,{"disambiguationData":[OSD([sQuery(id+"F0.wireOp",EDGE,"E0"),sQuery(id+"F0.wireOp",EDGE,"E1"),sQuery(id+"F0.wireOp",EDGE,"E2"),sQuery(id+"F0.wireOp",EDGE,"E3"),sQuery(id+"F0.wireOp",EDGE,"E4"),sQuery(id+"F0.wireOp",EDGE,"E5"),sQuery(id+"F0.wireOp",EDGE,"E6"),sQuery(id+"F0.wireOp",EDGE,"E7"),subQ0,sQuery(id+"F0.wireOp",EDGE,"E9"),sQuery(id+"F0.wireOp",EDGE,"E10"),sQuery(id+"F0.wireOp",EDGE,"E11"),sQuery(id+"F0.wireOp",EDGE,"E12"),sQuery(id+"F0.wireOp",EDGE,"E13"),sQuery(id+"F0.wireOp",EDGE,"eY3Ntxxg-AOvC-6Sjp-1Sg7-Dh78Z1ENxIpH"),sQuery(id+"F0.wireOp",EDGE,"MyhiPNTX-cIqE-LlnS-pzt5-9fsmOIbbkCBx"),sQuery(id+"F0.wireOp",EDGE,"c5fDbUR1-X0vD-gyia-IhE2-5vfisiyByv1Z"),sQuery(id+"F0.wireOp",EDGE,"z3w7DU23-CNS4-8nrn-3kLT-20PgSTqFnzF7"),sQuery(id+"F0.wireOp",EDGE,"hVG7QURc-v0VO-WvcA-oFbQ-66XRPdHWUu1N"),sQuery(id+"F0.wireOp",EDGE,"sfXvGUbo-ry80-gNXO-uOhN-L8BNUFceVqag"),sQuery(id+"F0.wireOp",EDGE,"QFO76mAv-pKme-nUwV-aMAa-C3MPOYOEvzGl"),sQuery(id+"F0.wireOp",EDGE,"fpymSL76-tXuZ-IzAU-FBSV-KsOygqMtrIGQ"),sQuery(id+"F0.wireOp",EDGE,"9a1d0dfd-7d57-477c-bff2-5a3fdc463cc7.filletArc"),sQuery(id+"F0.wireOp",EDGE,"38622195-8d8f-4664-a9bd-1ddf4e6b9831.filletArc"),sQuery(id+"F0.wireOp",EDGE,"98761a0e-d686-4a46-9134-fa1f6f4434ea.filletArc"),sQuery(id+"F0.wireOp",EDGE,"828cccf2-c6bf-4f99-963a-41c4c980739f.filletArc"),sQuery(id+"F0.wireOp",EDGE,"103ca256-2ef9-437d-bf9e-3dfbfe53d8ef.filletArc"),sQuery(id+"F0.wireOp",EDGE,"ed541100-cfe0-4745-a776-ba2087af7cae.filletArc"),sQuery(id+"F0.wireOp",EDGE,"bcec124a-270f-4962-9b0e-bfe1ee30ba45.filletArc"),sQuery(id+"F0.wireOp",EDGE,"ffb815b5-0439-4a1d-8740-96b920259a73.filletArc")])],"isStart":false})],"blendedInto":[makeQuery(id+"F1.opExtrude","CAP_FACE",FACE,{"disambiguationData":[OSD([sQuery(id+"F0.wireOp",EDGE,"E0"),sQuery(id+"F0.wireOp",EDGE,"E1"),sQuery(id+"F0.wireOp",EDGE,"E2"),sQuery(id+"F0.wireOp",EDGE,"E3"),sQuery(id+"F0.wireOp",EDGE,"E4"),sQuery(id+"F0.wireOp",EDGE,"E5"),sQuery(id+"F0.wireOp",EDGE,"E6"),sQuery(id+"F0.wireOp",EDGE,"E7"),subQ0,sQuery(id+"F0.wireOp",EDGE,"E9"),sQuery(id+"F0.wireOp",EDGE,"E10"),sQuery(id+"F0.wireOp",EDGE,"E11"),sQuery(id+"F0.wireOp",EDGE,"E12"),sQuery(id+"F0.wireOp",EDGE,"E13"),sQuery(id+"F0.wireOp",EDGE,"eY3Ntxxg-AOvC-6Sjp-1Sg7-Dh78Z1ENxIpH"),sQuery(id+"F0.wireOp",EDGE,"MyhiPNTX-cIqE-LlnS-pzt5-9fsmOIbbkCBx"),sQuery(id+"F0.wireOp",EDGE,"c5fDbUR1-X0vD-gyia-IhE2-5vfisiyByv1Z"),sQuery(id+"F0.wireOp",EDGE,"z3w7DU23-CNS4-8nrn-3kLT-20PgSTqFnzF7"),sQuery(id+"F0.wireOp",EDGE,"hVG7QURc-v0VO-WvcA-oFbQ-66XRPdHWUu1N"),sQuery(id+"F0.wireOp",EDGE,"sfXvGUbo-ry80-gNXO-uOhN-L8BNUFceVqag"),sQuery(id+"F0.wireOp",EDGE,"QFO76mAv-pKme-nUwV-aMAa-C3MPOYOEvzGl"),sQuery(id+"F0.wireOp",EDGE,"fpymSL76-tXuZ-IzAU-FBSV-KsOygqMtrIGQ"),sQuery(id+"F0.wireOp",EDGE,"9a1d0dfd-7d57-477c-bff2-5a3fdc463cc7.filletArc"),sQuery(id+"F0.wireOp",EDGE,"38622195-8d8f-4664-a9bd-1ddf4e6b9831.filletArc"),sQuery(id+"F0.wireOp",EDGE,"98761a0e-d686-4a46-9134-fa1f6f4434ea.filletArc"),sQuery(id+"F0.wireOp",EDGE,"828cccf2-c6bf-4f99-963a-41c4c980739f.filletArc"),sQuery(id+"F0.wireOp",EDGE,"103ca256-2ef9-437d-bf9e-3dfbfe53d8ef.filletArc"),sQuery(id+"F0.wireOp",EDGE,"ed541100-cfe0-4745-a776-ba2087af7cae.filletArc"),sQuery(id+"F0.wireOp",EDGE,"bcec124a-270f-4962-9b0e-bfe1ee30ba45.filletArc"),sQuery(id+"F0.wireOp",EDGE,"ffb815b5-0439-4a1d-8740-96b920259a73.filletArc")])],"isStart":false})]});}
            fillet(context, id + "F24", {"entities" : qUnion([Q0, Q1, Q2, Q3]), "radius" : 3 * mm, "tangentPropagation" : true, "allowEdgeOverflow" : false});
        }
        {
            var Q0;
            {var subQ0=makeQuery(id+"F1.opExtrude","CAP_FACE",FACE,{"disambiguationData":[OSD([sQuery(id+"F0.wireOp",EDGE,"E0"),sQuery(id+"F0.wireOp",EDGE,"E1"),sQuery(id+"F0.wireOp",EDGE,"E2"),sQuery(id+"F0.wireOp",EDGE,"E3"),sQuery(id+"F0.wireOp",EDGE,"E4"),sQuery(id+"F0.wireOp",EDGE,"E5"),sQuery(id+"F0.wireOp",EDGE,"E6"),sQuery(id+"F0.wireOp",EDGE,"E7"),sQuery(id+"F0.wireOp",EDGE,"E8"),sQuery(id+"F0.wireOp",EDGE,"E9"),sQuery(id+"F0.wireOp",EDGE,"E10"),sQuery(id+"F0.wireOp",EDGE,"E11"),sQuery(id+"F0.wireOp",EDGE,"E12"),sQuery(id+"F0.wireOp",EDGE,"E13"),sQuery(id+"F0.wireOp",EDGE,"Ze1lcFJT-wXSP-p6Sp-ibzG-PLGItWCrLXdm"),sQuery(id+"F0.wireOp",EDGE,"LCGSbrbs-ELcM-2btd-Nxrq-0X5GcQ4YE41g"),sQuery(id+"F0.wireOp",EDGE,"LftxxQDg-wbQU-W9M1-Aj5u-4wwMhXT5RF4g"),sQuery(id+"F0.wireOp",EDGE,"TYH3NWJP-SDMf-QQyj-lhjL-s3Mkt6MxWAxo")])],"isStart":false});Q0=makeQuery(id+"F21.opChamfer","BLEND_EDGE",EDGE,{"blendedFrom":[makeQuery(id+"F3.boolean.opBoolean","INTERSECT",EDGE,{"derivedFrom":[subQ0,makeQuery(id+"F3.opExtrude","CAP_FACE",FACE,{"disambiguationData":[OSD([sQuery(id+"F2.wireOp",EDGE,"E22.bottom"),sQuery(id+"F2.wireOp",EDGE,"E22.top"),sQuery(id+"F2.wireOp",EDGE,"E22.left"),sQuery(id+"F2.wireOp",EDGE,"E22.right")])],"isStart":false})]}),subQ0],"blendedInto":[subQ0]});}
            fillet(context, id + "F25", {"entities" : qUnion([Q0]), "radius" : 2.5 * mm, "tangentPropagation" : true, "allowEdgeOverflow" : false});
        }
        {
            var Q0;
            {var subQ0=sQuery(id+"F2.wireOp",EDGE,"E22.top");Q0=makeQuery(id+"F21.opChamfer","BLEND_EDGE",EDGE,{"blendedFrom":[makeQuery(id+"F3.boolean.opBoolean","INTERSECT",EDGE,{"derivedFrom":[makeQuery(id+"F1.opExtrude","CAP_FACE",FACE,{"disambiguationData":[OSD([sQuery(id+"F0.wireOp",EDGE,"E0"),sQuery(id+"F0.wireOp",EDGE,"E1"),sQuery(id+"F0.wireOp",EDGE,"E2"),sQuery(id+"F0.wireOp",EDGE,"E3"),sQuery(id+"F0.wireOp",EDGE,"E4"),sQuery(id+"F0.wireOp",EDGE,"E5"),sQuery(id+"F0.wireOp",EDGE,"E6"),sQuery(id+"F0.wireOp",EDGE,"E7"),sQuery(id+"F0.wireOp",EDGE,"E8"),sQuery(id+"F0.wireOp",EDGE,"E9"),sQuery(id+"F0.wireOp",EDGE,"E10"),sQuery(id+"F0.wireOp",EDGE,"E11"),sQuery(id+"F0.wireOp",EDGE,"E12"),sQuery(id+"F0.wireOp",EDGE,"E13"),sQuery(id+"F0.wireOp",EDGE,"eY3Ntxxg-AOvC-6Sjp-1Sg7-Dh78Z1ENxIpH"),sQuery(id+"F0.wireOp",EDGE,"MyhiPNTX-cIqE-LlnS-pzt5-9fsmOIbbkCBx"),sQuery(id+"F0.wireOp",EDGE,"c5fDbUR1-X0vD-gyia-IhE2-5vfisiyByv1Z"),sQuery(id+"F0.wireOp",EDGE,"z3w7DU23-CNS4-8nrn-3kLT-20PgSTqFnzF7"),sQuery(id+"F0.wireOp",EDGE,"hVG7QURc-v0VO-WvcA-oFbQ-66XRPdHWUu1N"),sQuery(id+"F0.wireOp",EDGE,"sfXvGUbo-ry80-gNXO-uOhN-L8BNUFceVqag"),sQuery(id+"F0.wireOp",EDGE,"QFO76mAv-pKme-nUwV-aMAa-C3MPOYOEvzGl"),sQuery(id+"F0.wireOp",EDGE,"fpymSL76-tXuZ-IzAU-FBSV-KsOygqMtrIGQ"),sQuery(id+"F0.wireOp",EDGE,"9a1d0dfd-7d57-477c-bff2-5a3fdc463cc7.filletArc"),sQuery(id+"F0.wireOp",EDGE,"38622195-8d8f-4664-a9bd-1ddf4e6b9831.filletArc"),sQuery(id+"F0.wireOp",EDGE,"98761a0e-d686-4a46-9134-fa1f6f4434ea.filletArc"),sQuery(id+"F0.wireOp",EDGE,"828cccf2-c6bf-4f99-963a-41c4c980739f.filletArc"),sQuery(id+"F0.wireOp",EDGE,"103ca256-2ef9-437d-bf9e-3dfbfe53d8ef.filletArc"),sQuery(id+"F0.wireOp",EDGE,"ed541100-cfe0-4745-a776-ba2087af7cae.filletArc"),sQuery(id+"F0.wireOp",EDGE,"bcec124a-270f-4962-9b0e-bfe1ee30ba45.filletArc"),sQuery(id+"F0.wireOp",EDGE,"ffb815b5-0439-4a1d-8740-96b920259a73.filletArc")])],"isStart":false}),makeQuery(id+"F3.opExtrude","CAP_FACE",FACE,{"disambiguationData":[OSD([sQuery(id+"F2.wireOp",EDGE,"E22.bottom"),subQ0,sQuery(id+"F2.wireOp",EDGE,"E22.left"),sQuery(id+"F2.wireOp",EDGE,"E22.right")])],"isStart":false})]}),makeQuery(id+"F3.boolean.opBoolean","COPY",FACE,{"derivedFrom":makeQuery(id+"F3.opExtrude","SWEPT_FACE",FACE,{"disambiguationData":[OSD([subQ0])]})})],"blendedInto":[makeQuery(id+"F3.boolean.opBoolean","COPY",FACE,{"derivedFrom":makeQuery(id+"F3.opExtrude","SWEPT_FACE",FACE,{"disambiguationData":[OSD([subQ0])]})})]});}
            var Q1;
            {var subQ0=sQuery(id+"F2.wireOp",EDGE,"E22.right");var subQ1=sQuery(id+"F2.wireOp",EDGE,"E22.left");var subQ2=sQuery(id+"F2.wireOp",EDGE,"E22.top");var subQ3=makeQuery(id+"F3.opExtrude","CAP_FACE",FACE,{"disambiguationData":[OSD([sQuery(id+"F2.wireOp",EDGE,"E22.bottom"),subQ2,subQ1,subQ0])],"isStart":true});Q1=makeQuery(id+"F21.opChamfer","BLEND_EDGE",EDGE,{"blendedFrom":[makeQuery(id+"F3.boolean.opBoolean","INTERSECT",EDGE,{"derivedFrom":[makeQuery(id+"F1.opExtrude","CAP_FACE",FACE,{"disambiguationData":[OSD([sQuery(id+"F0.wireOp",EDGE,"E0"),sQuery(id+"F0.wireOp",EDGE,"E1"),sQuery(id+"F0.wireOp",EDGE,"E2"),sQuery(id+"F0.wireOp",EDGE,"E3"),sQuery(id+"F0.wireOp",EDGE,"E4"),sQuery(id+"F0.wireOp",EDGE,"E5"),sQuery(id+"F0.wireOp",EDGE,"E6"),sQuery(id+"F0.wireOp",EDGE,"E7"),sQuery(id+"F0.wireOp",EDGE,"E8"),sQuery(id+"F0.wireOp",EDGE,"E9"),sQuery(id+"F0.wireOp",EDGE,"E10"),sQuery(id+"F0.wireOp",EDGE,"E11"),sQuery(id+"F0.wireOp",EDGE,"E12"),sQuery(id+"F0.wireOp",EDGE,"E13"),sQuery(id+"F0.wireOp",EDGE,"Ze1lcFJT-wXSP-p6Sp-ibzG-PLGItWCrLXdm"),sQuery(id+"F0.wireOp",EDGE,"LCGSbrbs-ELcM-2btd-Nxrq-0X5GcQ4YE41g"),sQuery(id+"F0.wireOp",EDGE,"LftxxQDg-wbQU-W9M1-Aj5u-4wwMhXT5RF4g"),sQuery(id+"F0.wireOp",EDGE,"TYH3NWJP-SDMf-QQyj-lhjL-s3Mkt6MxWAxo")])],"isStart":false}),subQ3]}),makeQuery(id+"F11.boolean.opBoolean","SPLIT",FACE,{"disambiguationData":[TD([makeQuery(id+"F11.opExtrude","SWEPT_FACE",FACE,{"disambiguationData":[OSD([sQuery(id+"F10.wireOp",EDGE,"E72.bottom")])]})])],"derivedFrom":makeQuery(id+"F3.boolean.opBoolean","COPY",FACE,{"derivedFrom":makeQuery(id+"F3.opExtrude","SWEPT_FACE",FACE,{"disambiguationData":[OSD([subQ2])]})})})],"blendedInto":[makeQuery(id+"F11.boolean.opBoolean","SPLIT",FACE,{"disambiguationData":[TD([makeQuery(id+"F11.opExtrude","SWEPT_FACE",FACE,{"disambiguationData":[OSD([sQuery(id+"F10.wireOp",EDGE,"E72.bottom")])]})])],"derivedFrom":makeQuery(id+"F3.boolean.opBoolean","COPY",FACE,{"derivedFrom":makeQuery(id+"F3.opExtrude","SWEPT_FACE",FACE,{"disambiguationData":[OSD([subQ2])]})})})]});}
            fillet(context, id + "F26", {"entities" : qUnion([Q0, Q1]), "radius" : 1 * mm, "tangentPropagation" : true, "allowEdgeOverflow" : false});
        }
        {
            var Q0;
            Q0=makeQuery(id+"F7.boolean.opBoolean","COPY",EDGE,{"derivedFrom":makeQuery(id+"F7.opExtrude","SWEPT_EDGE",EDGE,{"disambiguationData":[OSD([sQuery(id+"F6.wireOp",EDGE,"E40.MirrorCS"),sQuery(id+"F6.wireOp",EDGE,"E51.MirrorCS")])]})});
            var Q1;
            Q1=makeQuery(id+"F7.boolean.opBoolean","COPY",EDGE,{"derivedFrom":makeQuery(id+"F7.opExtrude","SWEPT_EDGE",EDGE,{"disambiguationData":[OSD([sQuery(id+"F6.wireOp",EDGE,"E46.MirrorCS"),sQuery(id+"F6.wireOp",EDGE,"E51.MirrorCS")])]})});
            var Q2;
            Q2=makeQuery(id+"F7.boolean.opBoolean","COPY",EDGE,{"derivedFrom":makeQuery(id+"F7.opExtrude","SWEPT_EDGE",EDGE,{"disambiguationData":[OSD([sQuery(id+"F6.wireOp",EDGE,"E46.MirrorCS"),sQuery(id+"F6.wireOp",EDGE,"E50.MirrorCS")])]})});
            var Q3;
            Q3=makeQuery(id+"F7.boolean.opBoolean","COPY",EDGE,{"derivedFrom":makeQuery(id+"F7.opExtrude","SWEPT_EDGE",EDGE,{"disambiguationData":[OSD([sQuery(id+"F6.wireOp",EDGE,"E43.MirrorCS"),sQuery(id+"F6.wireOp",EDGE,"E50.MirrorCS")])]})});
            var Q4;
            Q4=makeQuery(id+"F7.boolean.opBoolean","COPY",EDGE,{"derivedFrom":makeQuery(id+"F7.opExtrude","SWEPT_EDGE",EDGE,{"disambiguationData":[OSD([sQuery(id+"F6.wireOp",EDGE,"E42.MirrorCS"),sQuery(id+"F6.wireOp",EDGE,"E43.MirrorCS")])]})});
            var Q5;
            Q5=makeQuery(id+"F7.boolean.opBoolean","COPY",EDGE,{"derivedFrom":makeQuery(id+"F7.opExtrude","SWEPT_EDGE",EDGE,{"disambiguationData":[OSD([sQuery(id+"F6.wireOp",EDGE,"E40.MirrorCS"),sQuery(id+"F6.wireOp",EDGE,"E42.MirrorCS")])]})});
            var Q6;
            Q6=makeQuery(id+"F7.boolean.opBoolean","COPY",EDGE,{"derivedFrom":makeQuery(id+"F7.opExtrude","SWEPT_EDGE",EDGE,{"disambiguationData":[OSD([sQuery(id+"F6.wireOp",EDGE,"E44.MirrorCS"),sQuery(id+"F6.wireOp",EDGE,"E48.MirrorCS")])]})});
            var Q7;
            Q7=makeQuery(id+"F7.boolean.opBoolean","COPY",EDGE,{"derivedFrom":makeQuery(id+"F7.opExtrude","SWEPT_EDGE",EDGE,{"disambiguationData":[OSD([sQuery(id+"F6.wireOp",EDGE,"E47.MirrorCS"),sQuery(id+"F6.wireOp",EDGE,"E48.MirrorCS")])]})});
            var Q8;
            Q8=makeQuery(id+"F7.boolean.opBoolean","COPY",EDGE,{"derivedFrom":makeQuery(id+"F7.opExtrude","SWEPT_EDGE",EDGE,{"disambiguationData":[OSD([sQuery(id+"F6.wireOp",EDGE,"E44.MirrorCS"),sQuery(id+"F6.wireOp",EDGE,"E49.MirrorCS")])]})});
            var Q9;
            Q9=makeQuery(id+"F7.boolean.opBoolean","COPY",EDGE,{"derivedFrom":makeQuery(id+"F7.opExtrude","SWEPT_EDGE",EDGE,{"disambiguationData":[OSD([sQuery(id+"F6.wireOp",EDGE,"E41.MirrorCS"),sQuery(id+"F6.wireOp",EDGE,"E49.MirrorCS")])]})});
            var Q10;
            Q10=makeQuery(id+"F7.boolean.opBoolean","COPY",EDGE,{"derivedFrom":makeQuery(id+"F7.opExtrude","SWEPT_EDGE",EDGE,{"disambiguationData":[OSD([sQuery(id+"F6.wireOp",EDGE,"E41.MirrorCS"),sQuery(id+"F6.wireOp",EDGE,"E45.MirrorCS")])]})});
            var Q11;
            Q11=makeQuery(id+"F7.boolean.opBoolean","COPY",EDGE,{"derivedFrom":makeQuery(id+"F7.opExtrude","SWEPT_EDGE",EDGE,{"disambiguationData":[OSD([sQuery(id+"F6.wireOp",EDGE,"E45.MirrorCS"),sQuery(id+"F6.wireOp",EDGE,"E47.MirrorCS")])]})});
            var Q12;
            Q12=makeQuery(id+"F7.boolean.opBoolean","COPY",EDGE,{"derivedFrom":makeQuery(id+"F7.opExtrude","SWEPT_EDGE",EDGE,{"disambiguationData":[OSD([sQuery(id+"F6.wireOp",EDGE,"E34.MirrorCS"),sQuery(id+"F6.wireOp",EDGE,"E38.MirrorCS")])]})});
            var Q13;
            Q13=makeQuery(id+"F7.boolean.opBoolean","COPY",EDGE,{"derivedFrom":makeQuery(id+"F7.opExtrude","SWEPT_EDGE",EDGE,{"disambiguationData":[OSD([sQuery(id+"F6.wireOp",EDGE,"E34.MirrorCS"),sQuery(id+"F6.wireOp",EDGE,"E35.MirrorCS")])]})});
            var Q14;
            Q14=makeQuery(id+"F7.boolean.opBoolean","COPY",EDGE,{"derivedFrom":makeQuery(id+"F7.opExtrude","SWEPT_EDGE",EDGE,{"disambiguationData":[OSD([sQuery(id+"F6.wireOp",EDGE,"E35.MirrorCS"),sQuery(id+"F6.wireOp",EDGE,"E36.MirrorCS")])]})});
            var Q15;
            Q15=makeQuery(id+"F7.boolean.opBoolean","COPY",EDGE,{"derivedFrom":makeQuery(id+"F7.opExtrude","SWEPT_EDGE",EDGE,{"disambiguationData":[OSD([sQuery(id+"F6.wireOp",EDGE,"E36.MirrorCS"),sQuery(id+"F6.wireOp",EDGE,"E39.MirrorCS")])]})});
            var Q16;
            Q16=makeQuery(id+"F7.boolean.opBoolean","COPY",EDGE,{"derivedFrom":makeQuery(id+"F7.opExtrude","SWEPT_EDGE",EDGE,{"disambiguationData":[OSD([sQuery(id+"F6.wireOp",EDGE,"E37.MirrorCS"),sQuery(id+"F6.wireOp",EDGE,"E39.MirrorCS")])]})});
            var Q17;
            Q17=makeQuery(id+"F7.boolean.opBoolean","COPY",EDGE,{"derivedFrom":makeQuery(id+"F7.opExtrude","SWEPT_EDGE",EDGE,{"disambiguationData":[OSD([sQuery(id+"F6.wireOp",EDGE,"E37.MirrorCS"),sQuery(id+"F6.wireOp",EDGE,"E38.MirrorCS")])]})});
            var Q18;
            Q18=makeQuery(id+"F7.boolean.opBoolean","COPY",EDGE,{"derivedFrom":makeQuery(id+"F7.opExtrude","SWEPT_EDGE",EDGE,{"disambiguationData":[OSD([sQuery(id+"F6.wireOp",EDGE,"E29.2.0"),sQuery(id+"F6.wireOp",EDGE,"E30")])]})});
            var Q19;
            Q19=makeQuery(id+"F7.boolean.opBoolean","COPY",EDGE,{"derivedFrom":makeQuery(id+"F7.opExtrude","SWEPT_EDGE",EDGE,{"disambiguationData":[OSD([sQuery(id+"F6.wireOp",EDGE,"E29.2.0"),sQuery(id+"F6.wireOp",EDGE,"E31")])]})});
            var Q20;
            Q20=makeQuery(id+"F7.boolean.opBoolean","COPY",EDGE,{"derivedFrom":makeQuery(id+"F7.opExtrude","SWEPT_EDGE",EDGE,{"disambiguationData":[OSD([sQuery(id+"F6.wireOp",EDGE,"E28"),sQuery(id+"F6.wireOp",EDGE,"E31")])]})});
            var Q21;
            Q21=makeQuery(id+"F7.boolean.opBoolean","COPY",EDGE,{"derivedFrom":makeQuery(id+"F7.opExtrude","SWEPT_EDGE",EDGE,{"disambiguationData":[OSD([sQuery(id+"F6.wireOp",EDGE,"E28"),sQuery(id+"F6.wireOp",EDGE,"E32")])]})});
            var Q22;
            Q22=makeQuery(id+"F7.boolean.opBoolean","COPY",EDGE,{"derivedFrom":makeQuery(id+"F7.opExtrude","SWEPT_EDGE",EDGE,{"disambiguationData":[OSD([sQuery(id+"F6.wireOp",EDGE,"E29.1.0"),sQuery(id+"F6.wireOp",EDGE,"E32")])]})});
            var Q23;
            Q23=makeQuery(id+"F7.boolean.opBoolean","COPY",EDGE,{"derivedFrom":makeQuery(id+"F7.opExtrude","SWEPT_EDGE",EDGE,{"disambiguationData":[OSD([sQuery(id+"F6.wireOp",EDGE,"E29.1.0"),sQuery(id+"F6.wireOp",EDGE,"E30")])]})});
            var Q24;
            Q24=makeQuery(id+"F7.boolean.opBoolean","COPY",EDGE,{"derivedFrom":makeQuery(id+"F7.opExtrude","CAP_EDGE",EDGE,{"disambiguationData":[OSD([sQuery(id+"F6.wireOp",EDGE,"E27")])],"isStart":false})});
            var Q25;
            Q25=makeQuery(id+"F7.boolean.opBoolean","COPY",EDGE,{"derivedFrom":makeQuery(id+"F7.opExtrude","CAP_EDGE",EDGE,{"disambiguationData":[OSD([sQuery(id+"F6.wireOp",EDGE,"E52.MirrorC")])],"isStart":false})});
            var Q26;
            Q26=makeQuery(id+"F7.boolean.opBoolean","COPY",EDGE,{"derivedFrom":makeQuery(id+"F7.opExtrude","CAP_EDGE",EDGE,{"disambiguationData":[OSD([sQuery(id+"F6.wireOp",EDGE,"E53.MirrorC")])],"isStart":false})});
            var Q27;
            Q27=makeQuery(id+"F7.boolean.opBoolean","COPY",EDGE,{"derivedFrom":makeQuery(id+"F7.opExtrude","CAP_EDGE",EDGE,{"disambiguationData":[OSD([sQuery(id+"F6.wireOp",EDGE,"E33.MirrorC")])],"isStart":false})});
            fillet(context, id + "F27", {"entities" : qUnion([Q0, Q1, Q2, Q3, Q4, Q5, Q6, Q7, Q8, Q9, Q10, Q11, Q12, Q13, Q14, Q15, Q16, Q17, Q18, Q19, Q20, Q21, Q22, Q23, Q24, Q25, Q26, Q27]), "radius" : 1 * mm, "tangentPropagation" : true, "allowEdgeOverflow" : false});
        }
        {
            var Q0;
            Q0=makeQuery(id+"F7.boolean.opBoolean","COPY",FACE,{"derivedFrom":makeQuery(id+"F7.opExtrude","CAP_FACE",FACE,{"disambiguationData":[OSD([sQuery(id+"F6.wireOp",EDGE,"E40.MirrorCS"),sQuery(id+"F6.wireOp",EDGE,"E42.MirrorCS"),sQuery(id+"F6.wireOp",EDGE,"E43.MirrorCS"),sQuery(id+"F6.wireOp",EDGE,"E46.MirrorCS"),sQuery(id+"F6.wireOp",EDGE,"E50.MirrorCS"),sQuery(id+"F6.wireOp",EDGE,"E51.MirrorCS"),sQuery(id+"F6.wireOp",EDGE,"E52.MirrorC")])],"isStart":false})});
            var Q1;
            Q1=makeQuery(id+"F7.boolean.opBoolean","COPY",FACE,{"derivedFrom":makeQuery(id+"F7.opExtrude","CAP_FACE",FACE,{"disambiguationData":[OSD([sQuery(id+"F6.wireOp",EDGE,"E27"),sQuery(id+"F6.wireOp",EDGE,"E28"),sQuery(id+"F6.wireOp",EDGE,"E29.1.0"),sQuery(id+"F6.wireOp",EDGE,"E29.2.0"),sQuery(id+"F6.wireOp",EDGE,"E30"),sQuery(id+"F6.wireOp",EDGE,"E31"),sQuery(id+"F6.wireOp",EDGE,"E32")])],"isStart":false})});
            var Q2;
            Q2=makeQuery(id+"F7.boolean.opBoolean","COPY",FACE,{"derivedFrom":makeQuery(id+"F7.opExtrude","CAP_FACE",FACE,{"disambiguationData":[OSD([sQuery(id+"F6.wireOp",EDGE,"E33.MirrorC"),sQuery(id+"F6.wireOp",EDGE,"E34.MirrorCS"),sQuery(id+"F6.wireOp",EDGE,"E35.MirrorCS"),sQuery(id+"F6.wireOp",EDGE,"E36.MirrorCS"),sQuery(id+"F6.wireOp",EDGE,"E37.MirrorCS"),sQuery(id+"F6.wireOp",EDGE,"E38.MirrorCS"),sQuery(id+"F6.wireOp",EDGE,"E39.MirrorCS")])],"isStart":false})});
            var Q3;
            Q3=makeQuery(id+"F7.boolean.opBoolean","COPY",FACE,{"derivedFrom":makeQuery(id+"F7.opExtrude","CAP_FACE",FACE,{"disambiguationData":[OSD([sQuery(id+"F6.wireOp",EDGE,"E41.MirrorCS"),sQuery(id+"F6.wireOp",EDGE,"E44.MirrorCS"),sQuery(id+"F6.wireOp",EDGE,"E45.MirrorCS"),sQuery(id+"F6.wireOp",EDGE,"E47.MirrorCS"),sQuery(id+"F6.wireOp",EDGE,"E48.MirrorCS"),sQuery(id+"F6.wireOp",EDGE,"E49.MirrorCS"),sQuery(id+"F6.wireOp",EDGE,"E53.MirrorC")])],"isStart":false})});
            fillet(context, id + "F28", {"entities" : qUnion([Q0, Q1, Q2, Q3]), "radius" : .5 * mm, "tangentPropagation" : true, "allowEdgeOverflow" : false});
        }
        {
            var Q0;
            Q0=makeQuery(id+"F5.opExtrude","CAP_FACE",FACE,{"disambiguationData":[OSD([sQuery(id+"F4.wireOp",EDGE,"E25")])],"isStart":false});
            var Q1;
            Q1=makeQuery(id+"F5.opExtrude","CAP_FACE",FACE,{"disambiguationData":[OSD([sQuery(id+"F4.wireOp",EDGE,"E24")])],"isStart":false});
            var Q2;
            Q2=makeQuery(id+"F5.opExtrude","CAP_FACE",FACE,{"disambiguationData":[OSD([sQuery(id+"F4.wireOp",EDGE,"E23")])],"isStart":false});
            var Q3;
            Q3=makeQuery(id+"F5.opExtrude","CAP_FACE",FACE,{"disambiguationData":[OSD([sQuery(id+"F4.wireOp",EDGE,"E26")])],"isStart":false});
            fillet(context, id + "F29", {"entities" : qUnion([Q0, Q1, Q2, Q3]), "radius" : .9 * mm, "tangentPropagation" : true, "allowEdgeOverflow" : false});
        }
        {
            var Q0;
            {var subQ0=sQuery(id+"F0.wireOp",EDGE,"E13");var subQ1=makeQuery(id+"F5.boolean.opBoolean","MERGE",FACE,{"derivedFrom":[makeQuery(id+"F1.opExtrude","SWEPT_FACE",FACE,{"disambiguationData":[OSD([subQ0])]}),makeQuery(id+"F5.opExtrude","SWEPT_FACE",FACE,{"disambiguationData":[OSD([sQuery(id+"F4.wireOp",EDGE,"E26")])]})]});var subQ2=sQuery(id+"F0.wireOp",EDGE,"E2");Q0=makeQuery(id+"F24.opFillet","BLEND_EDGE",EDGE,{"blendedFrom":[makeQuery(id+"F22.opFillet","BLEND_EDGE",EDGE,{"blendedFrom":[makeQuery(id+"F19.opChamfer","BLEND_EDGE",EDGE,{"blendedFrom":[makeQuery(id+"F1.opExtrude","CAP_EDGE",EDGE,{"disambiguationData":[OSD([subQ2])],"isStart":false}),subQ1],"blendedInto":[subQ1]}),makeQuery(id+"F1.opExtrude","CAP_FACE",FACE,{"disambiguationData":[OSD([sQuery(id+"F0.wireOp",EDGE,"E0"),sQuery(id+"F0.wireOp",EDGE,"E1"),subQ2,sQuery(id+"F0.wireOp",EDGE,"E3"),sQuery(id+"F0.wireOp",EDGE,"E4"),sQuery(id+"F0.wireOp",EDGE,"E5"),sQuery(id+"F0.wireOp",EDGE,"E6"),sQuery(id+"F0.wireOp",EDGE,"E7"),sQuery(id+"F0.wireOp",EDGE,"E8"),sQuery(id+"F0.wireOp",EDGE,"E9"),sQuery(id+"F0.wireOp",EDGE,"E10"),sQuery(id+"F0.wireOp",EDGE,"E11"),sQuery(id+"F0.wireOp",EDGE,"E12"),subQ0,sQuery(id+"F0.wireOp",EDGE,"Ze1lcFJT-wXSP-p6Sp-ibzG-PLGItWCrLXdm"),sQuery(id+"F0.wireOp",EDGE,"LCGSbrbs-ELcM-2btd-Nxrq-0X5GcQ4YE41g"),sQuery(id+"F0.wireOp",EDGE,"LftxxQDg-wbQU-W9M1-Aj5u-4wwMhXT5RF4g"),sQuery(id+"F0.wireOp",EDGE,"TYH3NWJP-SDMf-QQyj-lhjL-s3Mkt6MxWAxo")])],"isStart":false})],"blendedInto":[makeQuery(id+"F1.opExtrude","CAP_FACE",FACE,{"disambiguationData":[OSD([sQuery(id+"F0.wireOp",EDGE,"E0"),sQuery(id+"F0.wireOp",EDGE,"E1"),subQ2,sQuery(id+"F0.wireOp",EDGE,"E3"),sQuery(id+"F0.wireOp",EDGE,"E4"),sQuery(id+"F0.wireOp",EDGE,"E5"),sQuery(id+"F0.wireOp",EDGE,"E6"),sQuery(id+"F0.wireOp",EDGE,"E7"),sQuery(id+"F0.wireOp",EDGE,"E8"),sQuery(id+"F0.wireOp",EDGE,"E9"),sQuery(id+"F0.wireOp",EDGE,"E10"),sQuery(id+"F0.wireOp",EDGE,"E11"),sQuery(id+"F0.wireOp",EDGE,"E12"),subQ0,sQuery(id+"F0.wireOp",EDGE,"Ze1lcFJT-wXSP-p6Sp-ibzG-PLGItWCrLXdm"),sQuery(id+"F0.wireOp",EDGE,"LCGSbrbs-ELcM-2btd-Nxrq-0X5GcQ4YE41g"),sQuery(id+"F0.wireOp",EDGE,"LftxxQDg-wbQU-W9M1-Aj5u-4wwMhXT5RF4g"),sQuery(id+"F0.wireOp",EDGE,"TYH3NWJP-SDMf-QQyj-lhjL-s3Mkt6MxWAxo")])],"isStart":false})]}),subQ1],"blendedInto":[subQ1]});}
            var Q1;
            {var subQ0=sQuery(id+"F0.wireOp",EDGE,"E10");var subQ1=makeQuery(id+"F5.boolean.opBoolean","MERGE",FACE,{"derivedFrom":[makeQuery(id+"F1.opExtrude","SWEPT_FACE",FACE,{"disambiguationData":[OSD([subQ0])]}),makeQuery(id+"F5.opExtrude","SWEPT_FACE",FACE,{"disambiguationData":[OSD([sQuery(id+"F4.wireOp",EDGE,"E23")])]})]});var subQ2=sQuery(id+"F0.wireOp",EDGE,"E4");Q1=makeQuery(id+"F24.opFillet","BLEND_EDGE",EDGE,{"blendedFrom":[makeQuery(id+"F22.opFillet","BLEND_EDGE",EDGE,{"blendedFrom":[makeQuery(id+"F19.opChamfer","BLEND_EDGE",EDGE,{"blendedFrom":[makeQuery(id+"F1.opExtrude","CAP_EDGE",EDGE,{"disambiguationData":[OSD([subQ2])],"isStart":false}),subQ1],"blendedInto":[subQ1]}),makeQuery(id+"F1.opExtrude","CAP_FACE",FACE,{"disambiguationData":[OSD([sQuery(id+"F0.wireOp",EDGE,"E0"),sQuery(id+"F0.wireOp",EDGE,"E1"),sQuery(id+"F0.wireOp",EDGE,"E2"),sQuery(id+"F0.wireOp",EDGE,"E3"),subQ2,sQuery(id+"F0.wireOp",EDGE,"E5"),sQuery(id+"F0.wireOp",EDGE,"E6"),sQuery(id+"F0.wireOp",EDGE,"E7"),sQuery(id+"F0.wireOp",EDGE,"E8"),sQuery(id+"F0.wireOp",EDGE,"E9"),subQ0,sQuery(id+"F0.wireOp",EDGE,"E11"),sQuery(id+"F0.wireOp",EDGE,"E12"),sQuery(id+"F0.wireOp",EDGE,"E13"),sQuery(id+"F0.wireOp",EDGE,"Ze1lcFJT-wXSP-p6Sp-ibzG-PLGItWCrLXdm"),sQuery(id+"F0.wireOp",EDGE,"LCGSbrbs-ELcM-2btd-Nxrq-0X5GcQ4YE41g"),sQuery(id+"F0.wireOp",EDGE,"LftxxQDg-wbQU-W9M1-Aj5u-4wwMhXT5RF4g"),sQuery(id+"F0.wireOp",EDGE,"TYH3NWJP-SDMf-QQyj-lhjL-s3Mkt6MxWAxo")])],"isStart":false})],"blendedInto":[makeQuery(id+"F1.opExtrude","CAP_FACE",FACE,{"disambiguationData":[OSD([sQuery(id+"F0.wireOp",EDGE,"E0"),sQuery(id+"F0.wireOp",EDGE,"E1"),sQuery(id+"F0.wireOp",EDGE,"E2"),sQuery(id+"F0.wireOp",EDGE,"E3"),subQ2,sQuery(id+"F0.wireOp",EDGE,"E5"),sQuery(id+"F0.wireOp",EDGE,"E6"),sQuery(id+"F0.wireOp",EDGE,"E7"),sQuery(id+"F0.wireOp",EDGE,"E8"),sQuery(id+"F0.wireOp",EDGE,"E9"),subQ0,sQuery(id+"F0.wireOp",EDGE,"E11"),sQuery(id+"F0.wireOp",EDGE,"E12"),sQuery(id+"F0.wireOp",EDGE,"E13"),sQuery(id+"F0.wireOp",EDGE,"Ze1lcFJT-wXSP-p6Sp-ibzG-PLGItWCrLXdm"),sQuery(id+"F0.wireOp",EDGE,"LCGSbrbs-ELcM-2btd-Nxrq-0X5GcQ4YE41g"),sQuery(id+"F0.wireOp",EDGE,"LftxxQDg-wbQU-W9M1-Aj5u-4wwMhXT5RF4g"),sQuery(id+"F0.wireOp",EDGE,"TYH3NWJP-SDMf-QQyj-lhjL-s3Mkt6MxWAxo")])],"isStart":false})]}),subQ1],"blendedInto":[subQ1]});}
            var Q2;
            {var subQ0=sQuery(id+"F0.wireOp",EDGE,"E11");var subQ1=makeQuery(id+"F5.boolean.opBoolean","MERGE",FACE,{"derivedFrom":[makeQuery(id+"F1.opExtrude","SWEPT_FACE",FACE,{"disambiguationData":[OSD([subQ0])]}),makeQuery(id+"F5.opExtrude","SWEPT_FACE",FACE,{"disambiguationData":[OSD([sQuery(id+"F4.wireOp",EDGE,"E24")])]})]});var subQ2=sQuery(id+"F0.wireOp",EDGE,"E9");Q2=makeQuery(id+"F24.opFillet","BLEND_EDGE",EDGE,{"blendedFrom":[makeQuery(id+"F22.opFillet","BLEND_EDGE",EDGE,{"blendedFrom":[makeQuery(id+"F19.opChamfer","BLEND_EDGE",EDGE,{"blendedFrom":[makeQuery(id+"F1.opExtrude","CAP_EDGE",EDGE,{"disambiguationData":[OSD([subQ2])],"isStart":false}),subQ1],"blendedInto":[subQ1]}),makeQuery(id+"F1.opExtrude","CAP_FACE",FACE,{"disambiguationData":[OSD([sQuery(id+"F0.wireOp",EDGE,"E0"),sQuery(id+"F0.wireOp",EDGE,"E1"),sQuery(id+"F0.wireOp",EDGE,"E2"),sQuery(id+"F0.wireOp",EDGE,"E3"),sQuery(id+"F0.wireOp",EDGE,"E4"),sQuery(id+"F0.wireOp",EDGE,"E5"),sQuery(id+"F0.wireOp",EDGE,"E6"),sQuery(id+"F0.wireOp",EDGE,"E7"),sQuery(id+"F0.wireOp",EDGE,"E8"),subQ2,sQuery(id+"F0.wireOp",EDGE,"E10"),subQ0,sQuery(id+"F0.wireOp",EDGE,"E12"),sQuery(id+"F0.wireOp",EDGE,"E13"),sQuery(id+"F0.wireOp",EDGE,"Ze1lcFJT-wXSP-p6Sp-ibzG-PLGItWCrLXdm"),sQuery(id+"F0.wireOp",EDGE,"LCGSbrbs-ELcM-2btd-Nxrq-0X5GcQ4YE41g"),sQuery(id+"F0.wireOp",EDGE,"LftxxQDg-wbQU-W9M1-Aj5u-4wwMhXT5RF4g"),sQuery(id+"F0.wireOp",EDGE,"TYH3NWJP-SDMf-QQyj-lhjL-s3Mkt6MxWAxo")])],"isStart":false})],"blendedInto":[makeQuery(id+"F1.opExtrude","CAP_FACE",FACE,{"disambiguationData":[OSD([sQuery(id+"F0.wireOp",EDGE,"E0"),sQuery(id+"F0.wireOp",EDGE,"E1"),sQuery(id+"F0.wireOp",EDGE,"E2"),sQuery(id+"F0.wireOp",EDGE,"E3"),sQuery(id+"F0.wireOp",EDGE,"E4"),sQuery(id+"F0.wireOp",EDGE,"E5"),sQuery(id+"F0.wireOp",EDGE,"E6"),sQuery(id+"F0.wireOp",EDGE,"E7"),sQuery(id+"F0.wireOp",EDGE,"E8"),subQ2,sQuery(id+"F0.wireOp",EDGE,"E10"),subQ0,sQuery(id+"F0.wireOp",EDGE,"E12"),sQuery(id+"F0.wireOp",EDGE,"E13"),sQuery(id+"F0.wireOp",EDGE,"Ze1lcFJT-wXSP-p6Sp-ibzG-PLGItWCrLXdm"),sQuery(id+"F0.wireOp",EDGE,"LCGSbrbs-ELcM-2btd-Nxrq-0X5GcQ4YE41g"),sQuery(id+"F0.wireOp",EDGE,"LftxxQDg-wbQU-W9M1-Aj5u-4wwMhXT5RF4g"),sQuery(id+"F0.wireOp",EDGE,"TYH3NWJP-SDMf-QQyj-lhjL-s3Mkt6MxWAxo")])],"isStart":false})]}),subQ1],"blendedInto":[subQ1]});}
            var Q3;
            {var subQ0=sQuery(id+"F0.wireOp",EDGE,"E12");var subQ1=makeQuery(id+"F5.boolean.opBoolean","MERGE",FACE,{"derivedFrom":[makeQuery(id+"F1.opExtrude","SWEPT_FACE",FACE,{"disambiguationData":[OSD([subQ0])]}),makeQuery(id+"F5.opExtrude","SWEPT_FACE",FACE,{"disambiguationData":[OSD([sQuery(id+"F4.wireOp",EDGE,"E25")])]})]});var subQ2=sQuery(id+"F0.wireOp",EDGE,"E3");Q3=makeQuery(id+"F24.opFillet","BLEND_EDGE",EDGE,{"blendedFrom":[makeQuery(id+"F22.opFillet","BLEND_EDGE",EDGE,{"blendedFrom":[makeQuery(id+"F19.opChamfer","BLEND_EDGE",EDGE,{"blendedFrom":[makeQuery(id+"F1.opExtrude","CAP_EDGE",EDGE,{"disambiguationData":[OSD([subQ2])],"isStart":false}),subQ1],"blendedInto":[subQ1]}),makeQuery(id+"F1.opExtrude","CAP_FACE",FACE,{"disambiguationData":[OSD([sQuery(id+"F0.wireOp",EDGE,"E0"),sQuery(id+"F0.wireOp",EDGE,"E1"),sQuery(id+"F0.wireOp",EDGE,"E2"),subQ2,sQuery(id+"F0.wireOp",EDGE,"E4"),sQuery(id+"F0.wireOp",EDGE,"E5"),sQuery(id+"F0.wireOp",EDGE,"E6"),sQuery(id+"F0.wireOp",EDGE,"E7"),sQuery(id+"F0.wireOp",EDGE,"E8"),sQuery(id+"F0.wireOp",EDGE,"E9"),sQuery(id+"F0.wireOp",EDGE,"E10"),sQuery(id+"F0.wireOp",EDGE,"E11"),subQ0,sQuery(id+"F0.wireOp",EDGE,"E13"),sQuery(id+"F0.wireOp",EDGE,"Ze1lcFJT-wXSP-p6Sp-ibzG-PLGItWCrLXdm"),sQuery(id+"F0.wireOp",EDGE,"LCGSbrbs-ELcM-2btd-Nxrq-0X5GcQ4YE41g"),sQuery(id+"F0.wireOp",EDGE,"LftxxQDg-wbQU-W9M1-Aj5u-4wwMhXT5RF4g"),sQuery(id+"F0.wireOp",EDGE,"TYH3NWJP-SDMf-QQyj-lhjL-s3Mkt6MxWAxo")])],"isStart":false})],"blendedInto":[makeQuery(id+"F1.opExtrude","CAP_FACE",FACE,{"disambiguationData":[OSD([sQuery(id+"F0.wireOp",EDGE,"E0"),sQuery(id+"F0.wireOp",EDGE,"E1"),sQuery(id+"F0.wireOp",EDGE,"E2"),subQ2,sQuery(id+"F0.wireOp",EDGE,"E4"),sQuery(id+"F0.wireOp",EDGE,"E5"),sQuery(id+"F0.wireOp",EDGE,"E6"),sQuery(id+"F0.wireOp",EDGE,"E7"),sQuery(id+"F0.wireOp",EDGE,"E8"),sQuery(id+"F0.wireOp",EDGE,"E9"),sQuery(id+"F0.wireOp",EDGE,"E10"),sQuery(id+"F0.wireOp",EDGE,"E11"),subQ0,sQuery(id+"F0.wireOp",EDGE,"E13"),sQuery(id+"F0.wireOp",EDGE,"Ze1lcFJT-wXSP-p6Sp-ibzG-PLGItWCrLXdm"),sQuery(id+"F0.wireOp",EDGE,"LCGSbrbs-ELcM-2btd-Nxrq-0X5GcQ4YE41g"),sQuery(id+"F0.wireOp",EDGE,"LftxxQDg-wbQU-W9M1-Aj5u-4wwMhXT5RF4g"),sQuery(id+"F0.wireOp",EDGE,"TYH3NWJP-SDMf-QQyj-lhjL-s3Mkt6MxWAxo")])],"isStart":false})]}),subQ1],"blendedInto":[subQ1]});}
            fillet(context, id + "F30", {"entities" : qUnion([Q0, Q1, Q2, Q3]), "radius" : 5 * mm, "tangentPropagation" : true, "allowEdgeOverflow" : false});
        }
        {
            var Q0;
            {var subQ0=sQuery(id+"F0.wireOp",EDGE,"E19");var subQ1=sQuery(id+"F0.wireOp",EDGE,"E17");Q0=makeQuery(id+"F15.boolean.opBoolean","MERGE",EDGE,{"derivedFrom":[makeQuery(id+"F1.opExtrude","SWEPT_EDGE",EDGE,{"disambiguationData":[OSD([subQ1,subQ0]),TDD([makeQuery(id+"F0.imprint","INTERSECT",VERTEX,{"disambiguationData":[OD(0.0)],"derivedFrom":[subQ1,subQ0]})])]})],"fromTools":[makeQuery(id+"F15.opExtrude","SWEPT_EDGE",EDGE,{"disambiguationData":[OSD([sQuery(id+"F14.wireOp",EDGE,"E87.MirrorCS"),sQuery(id+"F14.wireOp",EDGE,"E88.MirrorCS")])]})]});}
            var Q1;
            {var subQ0=sQuery(id+"F0.wireOp",EDGE,"E19");var subQ1=sQuery(id+"F0.wireOp",EDGE,"E17");Q1=makeQuery(id+"F15.boolean.opBoolean","MERGE",EDGE,{"derivedFrom":[makeQuery(id+"F1.opExtrude","SWEPT_EDGE",EDGE,{"disambiguationData":[OSD([subQ1,subQ0]),TDD([makeQuery(id+"F0.imprint","INTERSECT",VERTEX,{"disambiguationData":[OD(1.0)],"derivedFrom":[subQ1,subQ0]})])]})],"fromTools":[makeQuery(id+"F15.opExtrude","SWEPT_EDGE",EDGE,{"disambiguationData":[OSD([sQuery(id+"F14.wireOp",EDGE,"E86.MirrorCS"),sQuery(id+"F14.wireOp",EDGE,"E87.MirrorCS")])]})]});}
            var Q2;
            {var subQ0=sQuery(id+"F0.wireOp",EDGE,"E20");var subQ1=sQuery(id+"F0.wireOp",EDGE,"E18");Q2=makeQuery(id+"F15.boolean.opBoolean","MERGE",EDGE,{"derivedFrom":[makeQuery(id+"F1.opExtrude","SWEPT_EDGE",EDGE,{"disambiguationData":[OSD([subQ1,subQ0]),TDD([makeQuery(id+"F0.imprint","INTERSECT",VERTEX,{"disambiguationData":[OD(0.0)],"derivedFrom":[subQ1,subQ0]})])]})],"fromTools":[makeQuery(id+"F15.opExtrude","SWEPT_EDGE",EDGE,{"disambiguationData":[OSD([sQuery(id+"F14.wireOp",EDGE,"E90.MirrorCS"),sQuery(id+"F14.wireOp",EDGE,"E95.MirrorCS")])]})]});}
            var Q3;
            {var subQ0=sQuery(id+"F0.wireOp",EDGE,"E20");var subQ1=sQuery(id+"F0.wireOp",EDGE,"E18");Q3=makeQuery(id+"F15.boolean.opBoolean","MERGE",EDGE,{"derivedFrom":[makeQuery(id+"F1.opExtrude","SWEPT_EDGE",EDGE,{"disambiguationData":[OSD([subQ1,subQ0]),TDD([makeQuery(id+"F0.imprint","INTERSECT",VERTEX,{"disambiguationData":[OD(1.0)],"derivedFrom":[subQ1,subQ0]})])]})],"fromTools":[makeQuery(id+"F15.opExtrude","SWEPT_EDGE",EDGE,{"disambiguationData":[OSD([sQuery(id+"F14.wireOp",EDGE,"E90.MirrorCS"),sQuery(id+"F14.wireOp",EDGE,"E96.MirrorCS")])]})]});}
            var Q4;
            {var subQ0=sQuery(id+"F0.wireOp",EDGE,"E15");var subQ1=sQuery(id+"F0.wireOp",EDGE,"E14");Q4=makeQuery(id+"F15.boolean.opBoolean","MERGE",EDGE,{"derivedFrom":[makeQuery(id+"F1.opExtrude","SWEPT_EDGE",EDGE,{"disambiguationData":[OSD([subQ1,subQ0]),TDD([makeQuery(id+"F0.imprint","INTERSECT",VERTEX,{"disambiguationData":[OD(1.0)],"derivedFrom":[subQ1,subQ0]})])]})],"fromTools":[makeQuery(id+"F15.opExtrude","SWEPT_EDGE",EDGE,{"disambiguationData":[OSD([sQuery(id+"F14.wireOp",EDGE,"E83"),sQuery(id+"F14.wireOp",EDGE,"E84")])]})]});}
            var Q5;
            {var subQ0=sQuery(id+"F0.wireOp",EDGE,"E15");var subQ1=sQuery(id+"F0.wireOp",EDGE,"E14");Q5=makeQuery(id+"F15.boolean.opBoolean","MERGE",EDGE,{"derivedFrom":[makeQuery(id+"F1.opExtrude","SWEPT_EDGE",EDGE,{"disambiguationData":[OSD([subQ1,subQ0]),TDD([makeQuery(id+"F0.imprint","INTERSECT",VERTEX,{"disambiguationData":[OD(0.0)],"derivedFrom":[subQ1,subQ0]})])]})],"fromTools":[makeQuery(id+"F15.opExtrude","SWEPT_EDGE",EDGE,{"disambiguationData":[OSD([sQuery(id+"F14.wireOp",EDGE,"E81"),sQuery(id+"F14.wireOp",EDGE,"E84")])]})]});}
            var Q6;
            {var subQ0=sQuery(id+"F0.wireOp",EDGE,"E21");var subQ1=sQuery(id+"F0.wireOp",EDGE,"E16");Q6=makeQuery(id+"F15.boolean.opBoolean","MERGE",EDGE,{"derivedFrom":[makeQuery(id+"F1.opExtrude","SWEPT_EDGE",EDGE,{"disambiguationData":[OSD([subQ1,subQ0]),TDD([makeQuery(id+"F0.imprint","INTERSECT",VERTEX,{"disambiguationData":[OD(0.0)],"derivedFrom":[subQ1,subQ0]})])]})],"fromTools":[makeQuery(id+"F15.opExtrude","SWEPT_EDGE",EDGE,{"disambiguationData":[OSD([sQuery(id+"F14.wireOp",EDGE,"E89.MirrorCS"),sQuery(id+"F14.wireOp",EDGE,"E93.MirrorCS")])]})]});}
            var Q7;
            {var subQ0=sQuery(id+"F0.wireOp",EDGE,"E21");var subQ1=sQuery(id+"F0.wireOp",EDGE,"E16");Q7=makeQuery(id+"F15.boolean.opBoolean","MERGE",EDGE,{"derivedFrom":[makeQuery(id+"F1.opExtrude","SWEPT_EDGE",EDGE,{"disambiguationData":[OSD([subQ1,subQ0]),TDD([makeQuery(id+"F0.imprint","INTERSECT",VERTEX,{"disambiguationData":[OD(1.0)],"derivedFrom":[subQ1,subQ0]})])]})],"fromTools":[makeQuery(id+"F15.opExtrude","SWEPT_EDGE",EDGE,{"disambiguationData":[OSD([sQuery(id+"F14.wireOp",EDGE,"E89.MirrorCS"),sQuery(id+"F14.wireOp",EDGE,"E94.MirrorCS")])]})]});}
            fillet(context, id + "F31", {"entities" : qUnion([Q0, Q1, Q2, Q3, Q4, Q5, Q6, Q7]), "radius" : 5 * mm, "tangentPropagation" : true, "allowEdgeOverflow" : false});
        }
        {
            var Q0;
            Q0=makeQuery(id+"F16.opChamfer","BLEND_EDGE",EDGE,{"blendedFrom":[makeQuery(id+"F15.boolean.opBoolean","COPY",EDGE,{"derivedFrom":makeQuery(id+"F15.opExtrude","CAP_EDGE",EDGE,{"disambiguationData":[OSD([sQuery(id+"F14.wireOp",EDGE,"E84")])],"isStart":false})}),makeQuery(id+"F5.opExtrude","CAP_FACE",FACE,{"disambiguationData":[OSD([sQuery(id+"F4.wireOp",EDGE,"E26")])],"isStart":true})],"blendedInto":[makeQuery(id+"F5.opExtrude","CAP_FACE",FACE,{"disambiguationData":[OSD([sQuery(id+"F4.wireOp",EDGE,"E26")])],"isStart":true})]});
            var Q1;
            Q1=makeQuery(id+"F16.opChamfer","BLEND_EDGE",EDGE,{"blendedFrom":[makeQuery(id+"F15.boolean.opBoolean","COPY",EDGE,{"derivedFrom":makeQuery(id+"F15.opExtrude","CAP_EDGE",EDGE,{"disambiguationData":[OSD([sQuery(id+"F14.wireOp",EDGE,"E82")])],"isStart":false})}),makeQuery(id+"F1.opExtrude","CAP_FACE",FACE,{"disambiguationData":[OSD([sQuery(id+"F0.wireOp",EDGE,"E0"),sQuery(id+"F0.wireOp",EDGE,"E1"),sQuery(id+"F0.wireOp",EDGE,"E2"),sQuery(id+"F0.wireOp",EDGE,"E3"),sQuery(id+"F0.wireOp",EDGE,"E4"),sQuery(id+"F0.wireOp",EDGE,"E5"),sQuery(id+"F0.wireOp",EDGE,"E6"),sQuery(id+"F0.wireOp",EDGE,"E7"),sQuery(id+"F0.wireOp",EDGE,"E8"),sQuery(id+"F0.wireOp",EDGE,"E9"),sQuery(id+"F0.wireOp",EDGE,"E10"),sQuery(id+"F0.wireOp",EDGE,"E11"),sQuery(id+"F0.wireOp",EDGE,"E12"),sQuery(id+"F0.wireOp",EDGE,"E13"),sQuery(id+"F0.wireOp",EDGE,"E14"),sQuery(id+"F0.wireOp",EDGE,"E15"),sQuery(id+"F0.wireOp",EDGE,"E16"),sQuery(id+"F0.wireOp",EDGE,"E17"),sQuery(id+"F0.wireOp",EDGE,"E18"),sQuery(id+"F0.wireOp",EDGE,"E19"),sQuery(id+"F0.wireOp",EDGE,"E20"),sQuery(id+"F0.wireOp",EDGE,"E21")])],"isStart":true})],"blendedInto":[makeQuery(id+"F1.opExtrude","CAP_FACE",FACE,{"disambiguationData":[OSD([sQuery(id+"F0.wireOp",EDGE,"E0"),sQuery(id+"F0.wireOp",EDGE,"E1"),sQuery(id+"F0.wireOp",EDGE,"E2"),sQuery(id+"F0.wireOp",EDGE,"E3"),sQuery(id+"F0.wireOp",EDGE,"E4"),sQuery(id+"F0.wireOp",EDGE,"E5"),sQuery(id+"F0.wireOp",EDGE,"E6"),sQuery(id+"F0.wireOp",EDGE,"E7"),sQuery(id+"F0.wireOp",EDGE,"E8"),sQuery(id+"F0.wireOp",EDGE,"E9"),sQuery(id+"F0.wireOp",EDGE,"E10"),sQuery(id+"F0.wireOp",EDGE,"E11"),sQuery(id+"F0.wireOp",EDGE,"E12"),sQuery(id+"F0.wireOp",EDGE,"E13"),sQuery(id+"F0.wireOp",EDGE,"E14"),sQuery(id+"F0.wireOp",EDGE,"E15"),sQuery(id+"F0.wireOp",EDGE,"E16"),sQuery(id+"F0.wireOp",EDGE,"E17"),sQuery(id+"F0.wireOp",EDGE,"E18"),sQuery(id+"F0.wireOp",EDGE,"E19"),sQuery(id+"F0.wireOp",EDGE,"E20"),sQuery(id+"F0.wireOp",EDGE,"E21")])],"isStart":true})]});
            var Q2;
            Q2=makeQuery(id+"F16.opChamfer","BLEND_EDGE",EDGE,{"blendedFrom":[makeQuery(id+"F15.boolean.opBoolean","COPY",EDGE,{"derivedFrom":makeQuery(id+"F15.opExtrude","CAP_EDGE",EDGE,{"disambiguationData":[OSD([sQuery(id+"F14.wireOp",EDGE,"E89.MirrorCS")])],"isStart":false})}),makeQuery(id+"F5.opExtrude","CAP_FACE",FACE,{"disambiguationData":[OSD([sQuery(id+"F4.wireOp",EDGE,"E25")])],"isStart":true})],"blendedInto":[makeQuery(id+"F5.opExtrude","CAP_FACE",FACE,{"disambiguationData":[OSD([sQuery(id+"F4.wireOp",EDGE,"E25")])],"isStart":true})]});
            var Q3;
            Q3=makeQuery(id+"F16.opChamfer","BLEND_EDGE",EDGE,{"blendedFrom":[makeQuery(id+"F15.boolean.opBoolean","COPY",EDGE,{"derivedFrom":makeQuery(id+"F15.opExtrude","CAP_EDGE",EDGE,{"disambiguationData":[OSD([sQuery(id+"F14.wireOp",EDGE,"E91.MirrorCS")])],"isStart":false})}),makeQuery(id+"F1.opExtrude","CAP_FACE",FACE,{"disambiguationData":[OSD([sQuery(id+"F0.wireOp",EDGE,"E0"),sQuery(id+"F0.wireOp",EDGE,"E1"),sQuery(id+"F0.wireOp",EDGE,"E2"),sQuery(id+"F0.wireOp",EDGE,"E3"),sQuery(id+"F0.wireOp",EDGE,"E4"),sQuery(id+"F0.wireOp",EDGE,"E5"),sQuery(id+"F0.wireOp",EDGE,"E6"),sQuery(id+"F0.wireOp",EDGE,"E7"),sQuery(id+"F0.wireOp",EDGE,"E8"),sQuery(id+"F0.wireOp",EDGE,"E9"),sQuery(id+"F0.wireOp",EDGE,"E10"),sQuery(id+"F0.wireOp",EDGE,"E11"),sQuery(id+"F0.wireOp",EDGE,"E12"),sQuery(id+"F0.wireOp",EDGE,"E13"),sQuery(id+"F0.wireOp",EDGE,"E14"),sQuery(id+"F0.wireOp",EDGE,"E15"),sQuery(id+"F0.wireOp",EDGE,"E16"),sQuery(id+"F0.wireOp",EDGE,"E17"),sQuery(id+"F0.wireOp",EDGE,"E18"),sQuery(id+"F0.wireOp",EDGE,"E19"),sQuery(id+"F0.wireOp",EDGE,"E20"),sQuery(id+"F0.wireOp",EDGE,"E21")])],"isStart":true})],"blendedInto":[makeQuery(id+"F1.opExtrude","CAP_FACE",FACE,{"disambiguationData":[OSD([sQuery(id+"F0.wireOp",EDGE,"E0"),sQuery(id+"F0.wireOp",EDGE,"E1"),sQuery(id+"F0.wireOp",EDGE,"E2"),sQuery(id+"F0.wireOp",EDGE,"E3"),sQuery(id+"F0.wireOp",EDGE,"E4"),sQuery(id+"F0.wireOp",EDGE,"E5"),sQuery(id+"F0.wireOp",EDGE,"E6"),sQuery(id+"F0.wireOp",EDGE,"E7"),sQuery(id+"F0.wireOp",EDGE,"E8"),sQuery(id+"F0.wireOp",EDGE,"E9"),sQuery(id+"F0.wireOp",EDGE,"E10"),sQuery(id+"F0.wireOp",EDGE,"E11"),sQuery(id+"F0.wireOp",EDGE,"E12"),sQuery(id+"F0.wireOp",EDGE,"E13"),sQuery(id+"F0.wireOp",EDGE,"E14"),sQuery(id+"F0.wireOp",EDGE,"E15"),sQuery(id+"F0.wireOp",EDGE,"E16"),sQuery(id+"F0.wireOp",EDGE,"E17"),sQuery(id+"F0.wireOp",EDGE,"E18"),sQuery(id+"F0.wireOp",EDGE,"E19"),sQuery(id+"F0.wireOp",EDGE,"E20"),sQuery(id+"F0.wireOp",EDGE,"E21")])],"isStart":true})]});
            var Q4;
            Q4=makeQuery(id+"F16.opChamfer","BLEND_EDGE",EDGE,{"blendedFrom":[makeQuery(id+"F15.boolean.opBoolean","COPY",EDGE,{"derivedFrom":makeQuery(id+"F15.opExtrude","CAP_EDGE",EDGE,{"disambiguationData":[OSD([sQuery(id+"F14.wireOp",EDGE,"E87.MirrorCS")])],"isStart":false})}),makeQuery(id+"F5.opExtrude","CAP_FACE",FACE,{"disambiguationData":[OSD([sQuery(id+"F4.wireOp",EDGE,"E23")])],"isStart":true})],"blendedInto":[makeQuery(id+"F5.opExtrude","CAP_FACE",FACE,{"disambiguationData":[OSD([sQuery(id+"F4.wireOp",EDGE,"E23")])],"isStart":true})]});
            var Q5;
            Q5=makeQuery(id+"F16.opChamfer","BLEND_EDGE",EDGE,{"blendedFrom":[makeQuery(id+"F15.boolean.opBoolean","COPY",EDGE,{"derivedFrom":makeQuery(id+"F15.opExtrude","CAP_EDGE",EDGE,{"disambiguationData":[OSD([sQuery(id+"F14.wireOp",EDGE,"E85.MirrorCS")])],"isStart":false})}),makeQuery(id+"F1.opExtrude","CAP_FACE",FACE,{"disambiguationData":[OSD([sQuery(id+"F0.wireOp",EDGE,"E0"),sQuery(id+"F0.wireOp",EDGE,"E1"),sQuery(id+"F0.wireOp",EDGE,"E2"),sQuery(id+"F0.wireOp",EDGE,"E3"),sQuery(id+"F0.wireOp",EDGE,"E4"),sQuery(id+"F0.wireOp",EDGE,"E5"),sQuery(id+"F0.wireOp",EDGE,"E6"),sQuery(id+"F0.wireOp",EDGE,"E7"),sQuery(id+"F0.wireOp",EDGE,"E8"),sQuery(id+"F0.wireOp",EDGE,"E9"),sQuery(id+"F0.wireOp",EDGE,"E10"),sQuery(id+"F0.wireOp",EDGE,"E11"),sQuery(id+"F0.wireOp",EDGE,"E12"),sQuery(id+"F0.wireOp",EDGE,"E13"),sQuery(id+"F0.wireOp",EDGE,"E14"),sQuery(id+"F0.wireOp",EDGE,"E15"),sQuery(id+"F0.wireOp",EDGE,"E16"),sQuery(id+"F0.wireOp",EDGE,"E17"),sQuery(id+"F0.wireOp",EDGE,"E18"),sQuery(id+"F0.wireOp",EDGE,"E19"),sQuery(id+"F0.wireOp",EDGE,"E20"),sQuery(id+"F0.wireOp",EDGE,"E21")])],"isStart":true})],"blendedInto":[makeQuery(id+"F1.opExtrude","CAP_FACE",FACE,{"disambiguationData":[OSD([sQuery(id+"F0.wireOp",EDGE,"E0"),sQuery(id+"F0.wireOp",EDGE,"E1"),sQuery(id+"F0.wireOp",EDGE,"E2"),sQuery(id+"F0.wireOp",EDGE,"E3"),sQuery(id+"F0.wireOp",EDGE,"E4"),sQuery(id+"F0.wireOp",EDGE,"E5"),sQuery(id+"F0.wireOp",EDGE,"E6"),sQuery(id+"F0.wireOp",EDGE,"E7"),sQuery(id+"F0.wireOp",EDGE,"E8"),sQuery(id+"F0.wireOp",EDGE,"E9"),sQuery(id+"F0.wireOp",EDGE,"E10"),sQuery(id+"F0.wireOp",EDGE,"E11"),sQuery(id+"F0.wireOp",EDGE,"E12"),sQuery(id+"F0.wireOp",EDGE,"E13"),sQuery(id+"F0.wireOp",EDGE,"E14"),sQuery(id+"F0.wireOp",EDGE,"E15"),sQuery(id+"F0.wireOp",EDGE,"E16"),sQuery(id+"F0.wireOp",EDGE,"E17"),sQuery(id+"F0.wireOp",EDGE,"E18"),sQuery(id+"F0.wireOp",EDGE,"E19"),sQuery(id+"F0.wireOp",EDGE,"E20"),sQuery(id+"F0.wireOp",EDGE,"E21")])],"isStart":true})]});
            var Q6;
            Q6=makeQuery(id+"F16.opChamfer","BLEND_EDGE",EDGE,{"blendedFrom":[makeQuery(id+"F15.boolean.opBoolean","COPY",EDGE,{"derivedFrom":makeQuery(id+"F15.opExtrude","CAP_EDGE",EDGE,{"disambiguationData":[OSD([sQuery(id+"F14.wireOp",EDGE,"E90.MirrorCS")])],"isStart":false})}),makeQuery(id+"F5.opExtrude","CAP_FACE",FACE,{"disambiguationData":[OSD([sQuery(id+"F4.wireOp",EDGE,"E24")])],"isStart":true})],"blendedInto":[makeQuery(id+"F5.opExtrude","CAP_FACE",FACE,{"disambiguationData":[OSD([sQuery(id+"F4.wireOp",EDGE,"E24")])],"isStart":true})]});
            var Q7;
            Q7=makeQuery(id+"F16.opChamfer","BLEND_EDGE",EDGE,{"blendedFrom":[makeQuery(id+"F15.boolean.opBoolean","COPY",EDGE,{"derivedFrom":makeQuery(id+"F15.opExtrude","CAP_EDGE",EDGE,{"disambiguationData":[OSD([sQuery(id+"F14.wireOp",EDGE,"E92.MirrorCS")])],"isStart":false})}),makeQuery(id+"F1.opExtrude","CAP_FACE",FACE,{"disambiguationData":[OSD([sQuery(id+"F0.wireOp",EDGE,"E0"),sQuery(id+"F0.wireOp",EDGE,"E1"),sQuery(id+"F0.wireOp",EDGE,"E2"),sQuery(id+"F0.wireOp",EDGE,"E3"),sQuery(id+"F0.wireOp",EDGE,"E4"),sQuery(id+"F0.wireOp",EDGE,"E5"),sQuery(id+"F0.wireOp",EDGE,"E6"),sQuery(id+"F0.wireOp",EDGE,"E7"),sQuery(id+"F0.wireOp",EDGE,"E8"),sQuery(id+"F0.wireOp",EDGE,"E9"),sQuery(id+"F0.wireOp",EDGE,"E10"),sQuery(id+"F0.wireOp",EDGE,"E11"),sQuery(id+"F0.wireOp",EDGE,"E12"),sQuery(id+"F0.wireOp",EDGE,"E13"),sQuery(id+"F0.wireOp",EDGE,"E14"),sQuery(id+"F0.wireOp",EDGE,"E15"),sQuery(id+"F0.wireOp",EDGE,"E16"),sQuery(id+"F0.wireOp",EDGE,"E17"),sQuery(id+"F0.wireOp",EDGE,"E18"),sQuery(id+"F0.wireOp",EDGE,"E19"),sQuery(id+"F0.wireOp",EDGE,"E20"),sQuery(id+"F0.wireOp",EDGE,"E21")])],"isStart":true})],"blendedInto":[makeQuery(id+"F1.opExtrude","CAP_FACE",FACE,{"disambiguationData":[OSD([sQuery(id+"F0.wireOp",EDGE,"E0"),sQuery(id+"F0.wireOp",EDGE,"E1"),sQuery(id+"F0.wireOp",EDGE,"E2"),sQuery(id+"F0.wireOp",EDGE,"E3"),sQuery(id+"F0.wireOp",EDGE,"E4"),sQuery(id+"F0.wireOp",EDGE,"E5"),sQuery(id+"F0.wireOp",EDGE,"E6"),sQuery(id+"F0.wireOp",EDGE,"E7"),sQuery(id+"F0.wireOp",EDGE,"E8"),sQuery(id+"F0.wireOp",EDGE,"E9"),sQuery(id+"F0.wireOp",EDGE,"E10"),sQuery(id+"F0.wireOp",EDGE,"E11"),sQuery(id+"F0.wireOp",EDGE,"E12"),sQuery(id+"F0.wireOp",EDGE,"E13"),sQuery(id+"F0.wireOp",EDGE,"E14"),sQuery(id+"F0.wireOp",EDGE,"E15"),sQuery(id+"F0.wireOp",EDGE,"E16"),sQuery(id+"F0.wireOp",EDGE,"E17"),sQuery(id+"F0.wireOp",EDGE,"E18"),sQuery(id+"F0.wireOp",EDGE,"E19"),sQuery(id+"F0.wireOp",EDGE,"E20"),sQuery(id+"F0.wireOp",EDGE,"E21")])],"isStart":true})]});
            fillet(context, id + "F32", {"entities" : qUnion([Q0, Q1, Q2, Q3, Q4, Q5, Q6, Q7]), "radius" : 2 * mm, "tangentPropagation" : true, "allowEdgeOverflow" : false});
        }
        {
            var Q0;
            Q0=makeQuery(id+"F15.boolean.opBoolean","COPY",EDGE,{"derivedFrom":makeQuery(id+"F15.opExtrude","CAP_EDGE",EDGE,{"disambiguationData":[OSD([sQuery(id+"F14.wireOp",EDGE,"E88.MirrorCS")])],"isStart":true})});
            var Q1;
            Q1=makeQuery(id+"F15.boolean.opBoolean","COPY",EDGE,{"derivedFrom":makeQuery(id+"F15.opExtrude","CAP_EDGE",EDGE,{"disambiguationData":[OSD([sQuery(id+"F14.wireOp",EDGE,"E95.MirrorCS")])],"isStart":true})});
            var Q2;
            Q2=makeQuery(id+"F15.boolean.opBoolean","COPY",EDGE,{"derivedFrom":makeQuery(id+"F15.opExtrude","CAP_EDGE",EDGE,{"disambiguationData":[OSD([sQuery(id+"F14.wireOp",EDGE,"E81")])],"isStart":true})});
            var Q3;
            Q3=makeQuery(id+"F15.boolean.opBoolean","COPY",EDGE,{"derivedFrom":makeQuery(id+"F15.opExtrude","CAP_EDGE",EDGE,{"disambiguationData":[OSD([sQuery(id+"F14.wireOp",EDGE,"E93.MirrorCS")])],"isStart":true})});
            var Q4;
            Q4=makeQuery(id+"F16.opChamfer","BLEND_EDGE",EDGE,{"blendedFrom":[makeQuery(id+"F15.boolean.opBoolean","COPY",EDGE,{"derivedFrom":makeQuery(id+"F15.opExtrude","CAP_EDGE",EDGE,{"disambiguationData":[OSD([sQuery(id+"F14.wireOp",EDGE,"E82")])],"isStart":false})}),makeQuery(id+"F15.boolean.opBoolean","COPY",FACE,{"derivedFrom":makeQuery(id+"F15.opExtrude","SWEPT_FACE",FACE,{"disambiguationData":[OSD([sQuery(id+"F14.wireOp",EDGE,"E81")])]})})],"blendedInto":[makeQuery(id+"F15.boolean.opBoolean","COPY",FACE,{"derivedFrom":makeQuery(id+"F15.opExtrude","SWEPT_FACE",FACE,{"disambiguationData":[OSD([sQuery(id+"F14.wireOp",EDGE,"E81")])]})})]});
            var Q5;
            Q5=makeQuery(id+"F16.opChamfer","BLEND_EDGE",EDGE,{"blendedFrom":[makeQuery(id+"F15.boolean.opBoolean","COPY",EDGE,{"derivedFrom":makeQuery(id+"F15.opExtrude","CAP_EDGE",EDGE,{"disambiguationData":[OSD([sQuery(id+"F14.wireOp",EDGE,"E89.MirrorCS")])],"isStart":false})}),makeQuery(id+"F15.boolean.opBoolean","COPY",FACE,{"derivedFrom":makeQuery(id+"F15.opExtrude","SWEPT_FACE",FACE,{"disambiguationData":[OSD([sQuery(id+"F14.wireOp",EDGE,"E93.MirrorCS")])]})})],"blendedInto":[makeQuery(id+"F15.boolean.opBoolean","COPY",FACE,{"derivedFrom":makeQuery(id+"F15.opExtrude","SWEPT_FACE",FACE,{"disambiguationData":[OSD([sQuery(id+"F14.wireOp",EDGE,"E93.MirrorCS")])]})})]});
            var Q6;
            Q6=makeQuery(id+"F16.opChamfer","BLEND_EDGE",EDGE,{"blendedFrom":[makeQuery(id+"F15.boolean.opBoolean","COPY",EDGE,{"derivedFrom":makeQuery(id+"F15.opExtrude","CAP_EDGE",EDGE,{"disambiguationData":[OSD([sQuery(id+"F14.wireOp",EDGE,"E85.MirrorCS")])],"isStart":false})}),makeQuery(id+"F15.boolean.opBoolean","COPY",FACE,{"derivedFrom":makeQuery(id+"F15.opExtrude","SWEPT_FACE",FACE,{"disambiguationData":[OSD([sQuery(id+"F14.wireOp",EDGE,"E88.MirrorCS")])]})})],"blendedInto":[makeQuery(id+"F15.boolean.opBoolean","COPY",FACE,{"derivedFrom":makeQuery(id+"F15.opExtrude","SWEPT_FACE",FACE,{"disambiguationData":[OSD([sQuery(id+"F14.wireOp",EDGE,"E88.MirrorCS")])]})})]});
            var Q7;
            Q7=makeQuery(id+"F16.opChamfer","BLEND_EDGE",EDGE,{"blendedFrom":[makeQuery(id+"F15.boolean.opBoolean","COPY",EDGE,{"derivedFrom":makeQuery(id+"F15.opExtrude","CAP_EDGE",EDGE,{"disambiguationData":[OSD([sQuery(id+"F14.wireOp",EDGE,"E90.MirrorCS")])],"isStart":false})}),makeQuery(id+"F15.boolean.opBoolean","COPY",FACE,{"derivedFrom":makeQuery(id+"F15.opExtrude","SWEPT_FACE",FACE,{"disambiguationData":[OSD([sQuery(id+"F14.wireOp",EDGE,"E95.MirrorCS")])]})})],"blendedInto":[makeQuery(id+"F15.boolean.opBoolean","COPY",FACE,{"derivedFrom":makeQuery(id+"F15.opExtrude","SWEPT_FACE",FACE,{"disambiguationData":[OSD([sQuery(id+"F14.wireOp",EDGE,"E95.MirrorCS")])]})})]});
            fillet(context, id + "F33", {"entities" : qUnion([Q0, Q1, Q2, Q3, Q4, Q5, Q6, Q7]), "radius" : .5 * mm, "tangentPropagation" : true, "allowEdgeOverflow" : false});
        }
    });
